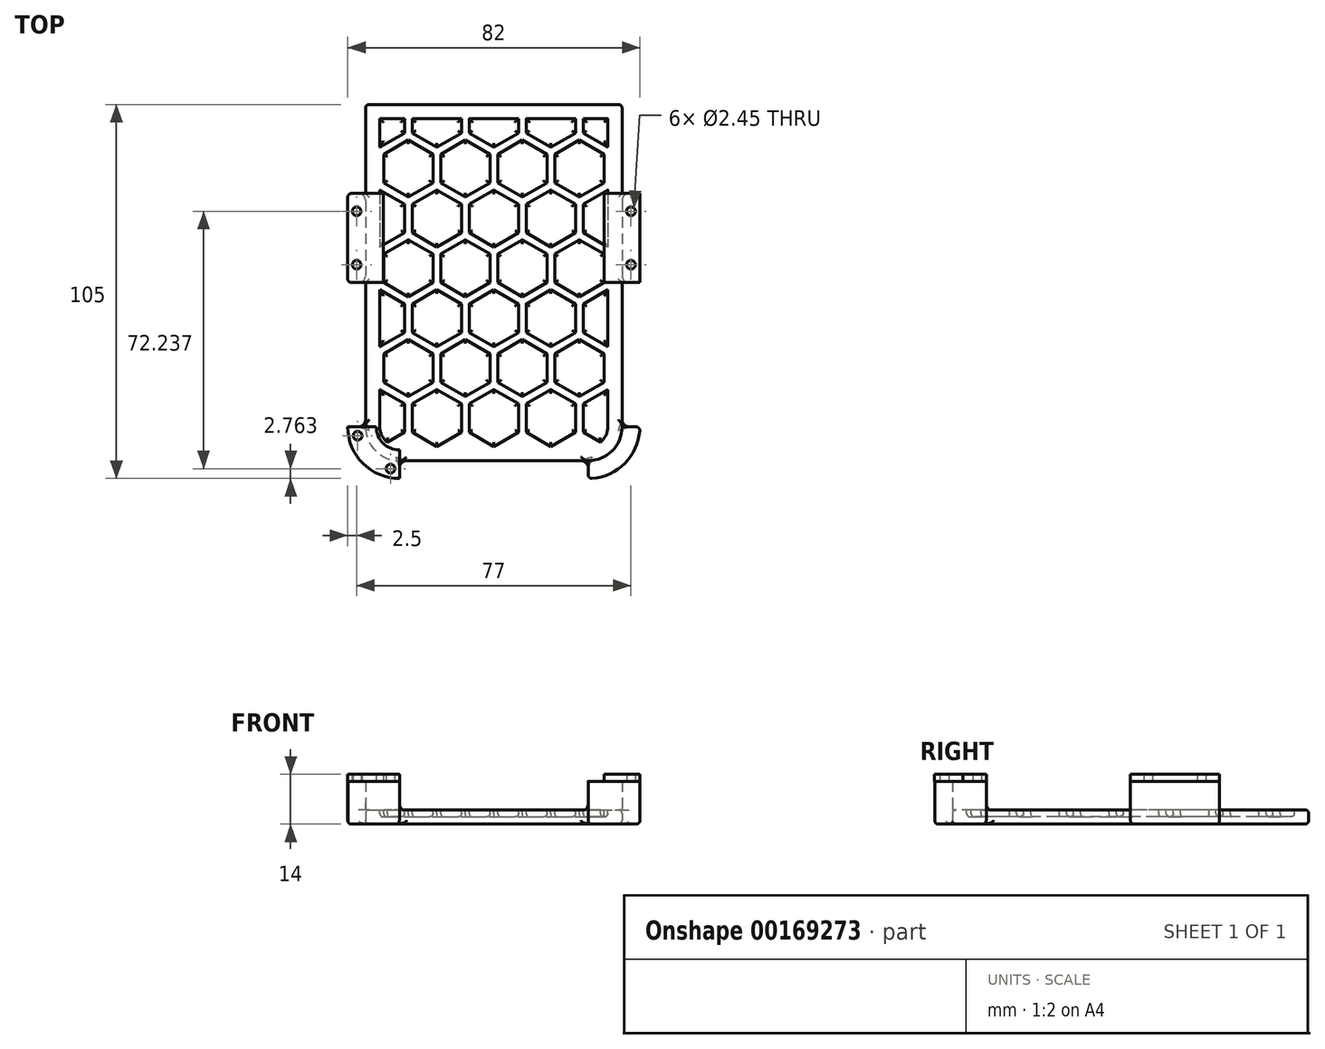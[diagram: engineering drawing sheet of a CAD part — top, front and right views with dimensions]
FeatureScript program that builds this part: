
annotation { "Feature Type Name" : "Feature", "Feature Type Description" : "" }
export const myFeature = defineFeature(function(context is Context, id is Id, definition is map)
    precondition{}
    {
        {
            var Q0;
            Q0=qCreatedBy(makeId("Top.planeOp"),FACE);
            var sketch = newSketch(context, id + "F0", { "sketchPlane" : qUnion([Q0])});
            skLineSegment(sketch, "E0.bottom", {"start": v(-36, 0) * mm, "end": v(36, 0) * mm});
            skLineSegment(sketch, "E0.top", {"start": v(-26.5, -100) * mm, "end": v(26.5, -100) * mm});
            skLineSegment(sketch, "E0.left", {"start": v(-36, 0) * mm, "end": v(-36, -90.5) * mm});
            skLineSegment(sketch, "E0.right", {"start": v(36, 0) * mm, "end": v(36, -90.5) * mm});
            skLineSegment(sketch, "E1", {"start": v(-36, -25) * mm, "end": v(-41, -25) * mm});
            skLineSegment(sketch, "E2", {"start": v(-41, -25) * mm, "end": v(-41, -50) * mm});
            skLineSegment(sketch, "E3", {"start": v(-41, -50) * mm, "end": v(-36, -50) * mm});
            skPoint(sketch, "E4.visualSharp", {"position": v(-36, -100) * mm});
            skArc(sketch, "E4.filletArc", {"start": v(-36, -90.5) * mm, "mid": v(-33.22, -97.22) * mm, "end": v(-26.5, -100) * mm});
            skPoint(sketch, "E5.visualSharp", {"position": v(36, -100) * mm});
            skArc(sketch, "E5.filletArc", {"start": v(26.5, -100) * mm, "mid": v(33.22, -97.22) * mm, "end": v(36, -90.5) * mm});
            skLineSegment(sketch, "E6", {"start": v(0, 0) * mm, "end": v(0, -100) * mm, "construction": true});
            skLineSegment(sketch, "E7.MirrorCS", {"start": v(36, -25) * mm, "end": v(41, -25) * mm});
            skLineSegment(sketch, "E8.MirrorCS", {"start": v(41, -25) * mm, "end": v(41, -50) * mm});
            skLineSegment(sketch, "E9.MirrorCS", {"start": v(41, -50) * mm, "end": v(36, -50) * mm});
            skArc(sketch, "E10.0", {"start": v(-41, -90.5) * mm, "mid": v(-36.75, -100.75) * mm, "end": v(-26.5, -105) * mm});
            skLineSegment(sketch, "E11", {"start": v(-41, -90.5) * mm, "end": v(-36, -90.5) * mm});
            skLineSegment(sketch, "E12", {"start": v(-26.5, -100) * mm, "end": v(-26.5, -105) * mm});
            skLineSegment(sketch, "E13.MirrorCS", {"start": v(26.5, -100) * mm, "end": v(26.5, -105) * mm});
            skArc(sketch, "E14.MirrorCS", {"start": v(41, -90.5) * mm, "mid": v(36.75, -100.75) * mm, "end": v(26.5, -105) * mm});
            skLineSegment(sketch, "E15.MirrorCS", {"start": v(41, -90.5) * mm, "end": v(36, -90.5) * mm});
            skSolve(sketch);
        }
        {
            var Q0;
            {var subQ3=sQuery(id+"F0.wireOp",EDGE,"E0.bottom");Q0=makeQuery(id+"F0.imprint","IMPRINT",FACE,{"disambiguationData":[TD([[makeQuery(id+"F0.imprint","IMPRINT",EDGE,{"derivedFrom":subQ3}),-1.0]])]});}
            extrude(context, id + "F1", {"entities" : qUnion([Q0]), "depth" : 4 * mm});
        }
        {
            var Q0;
            {var subQ0=sQuery(id+"F0.wireOp",EDGE,"E1");Q0=makeQuery(id+"F0.imprint","IMPRINT",FACE,{"disambiguationData":[TD([[makeQuery(id+"F0.imprint","IMPRINT",EDGE,{"derivedFrom":subQ0}),1.0]])]});}
            var Q1;
            Q1=makeQuery(id+"F0.imprint","IMPRINT",FACE,{"disambiguationData":[TD([[makeQuery(id+"F0.imprint","IMPRINT",EDGE,{"derivedFrom":sQuery(id+"F0.wireOp",EDGE,"E4.filletArc")}),-1.0]])]});
            var Q2;
            Q2=makeQuery(id+"F0.imprint","IMPRINT",FACE,{"disambiguationData":[TD([[makeQuery(id+"F0.imprint","IMPRINT",EDGE,{"derivedFrom":sQuery(id+"F0.wireOp",EDGE,"E5.filletArc")}),-1.0]])]});
            var Q3;
            {var subQ0=sQuery(id+"F0.wireOp",EDGE,"E7.MirrorCS");Q3=makeQuery(id+"F0.imprint","IMPRINT",FACE,{"disambiguationData":[TD([[makeQuery(id+"F0.imprint","IMPRINT",EDGE,{"derivedFrom":subQ0}),-1.0]])]});}
            extrude(context, id + "F2", {"entities" : qUnion([Q0, Q1, Q2, Q3]), "operationType" : NewBodyOperationType.ADD, "depth" : 12 * mm});
        }
        {
            var Q0;
            Q0=makeQuery(id+"F2.opExtrude","SWEPT_EDGE",EDGE,{"disambiguationData":[OSD([sQuery(id+"F0.wireOp",EDGE,"E2"),sQuery(id+"F0.wireOp",EDGE,"E3")])]});
            var Q1;
            Q1=makeQuery(id+"F2.opExtrude","SWEPT_EDGE",EDGE,{"disambiguationData":[OSD([sQuery(id+"F0.wireOp",EDGE,"E1"),sQuery(id+"F0.wireOp",EDGE,"E2")])]});
            var Q2;
            Q2=makeQuery(id+"F2.opExtrude","SWEPT_EDGE",EDGE,{"disambiguationData":[OSD([sQuery(id+"F0.wireOp",EDGE,"E10.0"),sQuery(id+"F0.wireOp",EDGE,"E11")])]});
            var Q3;
            Q3=makeQuery(id+"F2.opExtrude","SWEPT_EDGE",EDGE,{"disambiguationData":[OSD([sQuery(id+"F0.wireOp",EDGE,"E10.0"),sQuery(id+"F0.wireOp",EDGE,"E12")])]});
            var Q4;
            Q4=makeQuery(id+"F2.opExtrude","CAP_EDGE",EDGE,{"disambiguationData":[OSD([sQuery(id+"F0.wireOp",EDGE,"E10.0")])],"isStart":true});
            var Q5;
            Q5=makeQuery(id+"F2.opExtrude","CAP_EDGE",EDGE,{"disambiguationData":[OSD([sQuery(id+"F0.wireOp",EDGE,"E2")])],"isStart":true});
            var Q6;
            Q6=makeQuery(id+"F2.opExtrude","CAP_EDGE",EDGE,{"disambiguationData":[OSD([sQuery(id+"F0.wireOp",EDGE,"E14.MirrorCS")])],"isStart":true});
            var Q7;
            Q7=makeQuery(id+"F2.opExtrude","SWEPT_EDGE",EDGE,{"disambiguationData":[OSD([sQuery(id+"F0.wireOp",EDGE,"E13.MirrorCS"),sQuery(id+"F0.wireOp",EDGE,"E14.MirrorCS")])]});
            var Q8;
            Q8=makeQuery(id+"F2.opExtrude","SWEPT_EDGE",EDGE,{"disambiguationData":[OSD([sQuery(id+"F0.wireOp",EDGE,"E14.MirrorCS"),sQuery(id+"F0.wireOp",EDGE,"E15.MirrorCS")])]});
            var Q9;
            Q9=makeQuery(id+"F2.opExtrude","SWEPT_EDGE",EDGE,{"disambiguationData":[OSD([sQuery(id+"F0.wireOp",EDGE,"E8.MirrorCS"),sQuery(id+"F0.wireOp",EDGE,"E9.MirrorCS")])]});
            var Q10;
            Q10=makeQuery(id+"F2.opExtrude","SWEPT_EDGE",EDGE,{"disambiguationData":[OSD([sQuery(id+"F0.wireOp",EDGE,"E7.MirrorCS"),sQuery(id+"F0.wireOp",EDGE,"E8.MirrorCS")])]});
            var Q11;
            Q11=makeQuery(id+"F2.opExtrude","CAP_EDGE",EDGE,{"disambiguationData":[OSD([sQuery(id+"F0.wireOp",EDGE,"E8.MirrorCS")])],"isStart":true});
            var Q12;
            Q12=makeQuery(id+"F2.opExtrude","CAP_EDGE",EDGE,{"disambiguationData":[OSD([sQuery(id+"F0.wireOp",EDGE,"E9.MirrorCS")])],"isStart":true});
            var Q13;
            {var subQ1=sQuery(id+"F0.wireOp",EDGE,"E0.right");var subQ4=sQuery(id+"F0.wireOp",EDGE,"E0.bottom");Q13=makeQuery(id+"F2.boolean.opBoolean","SPLIT",EDGE,{"disambiguationData":[TD([makeQuery(id+"F1.opExtrude","SWEPT_FACE",FACE,{"disambiguationData":[OSD([subQ4])]})])],"derivedFrom":makeQuery(id+"F1.opExtrude","CAP_EDGE",EDGE,{"disambiguationData":[OSD([subQ1])],"isStart":true})});}
            var Q14;
            Q14=makeQuery(id+"F1.opExtrude","CAP_EDGE",EDGE,{"disambiguationData":[OSD([sQuery(id+"F0.wireOp",EDGE,"E0.top")])],"isStart":true});
            var Q15;
            {var subQ1=sQuery(id+"F0.wireOp",EDGE,"E0.left");var subQ2=sQuery(id+"F0.wireOp",EDGE,"E3");Q15=makeQuery(id+"F2.boolean.opBoolean","SPLIT",EDGE,{"disambiguationData":[TD([makeQuery(id+"F2.opExtrude","SWEPT_FACE",FACE,{"disambiguationData":[OSD([subQ2])]})])],"derivedFrom":makeQuery(id+"F1.opExtrude","CAP_EDGE",EDGE,{"disambiguationData":[OSD([subQ1])],"isStart":true})});}
            var Q16;
            Q16=makeQuery(id+"F2.opExtrude","CAP_EDGE",EDGE,{"disambiguationData":[OSD([sQuery(id+"F0.wireOp",EDGE,"E3")])],"isStart":true});
            var Q17;
            Q17=makeQuery(id+"F2.opExtrude","CAP_EDGE",EDGE,{"disambiguationData":[OSD([sQuery(id+"F0.wireOp",EDGE,"E1")])],"isStart":true});
            var Q18;
            Q18=makeQuery(id+"F1.opExtrude","SWEPT_EDGE",EDGE,{"disambiguationData":[OSD([sQuery(id+"F0.wireOp",EDGE,"E0.bottom"),sQuery(id+"F0.wireOp",EDGE,"E0.right")])]});
            var Q19;
            {var subQ0=sQuery(id+"F0.wireOp",EDGE,"E0.left");var subQ5=sQuery(id+"F0.wireOp",EDGE,"E0.bottom");Q19=makeQuery(id+"F2.boolean.opBoolean","SPLIT",EDGE,{"disambiguationData":[TD([makeQuery(id+"F1.opExtrude","SWEPT_FACE",FACE,{"disambiguationData":[OSD([subQ5])]})])],"derivedFrom":makeQuery(id+"F1.opExtrude","CAP_EDGE",EDGE,{"disambiguationData":[OSD([subQ0])],"isStart":true})});}
            var Q20;
            Q20=makeQuery(id+"F1.opExtrude","CAP_EDGE",EDGE,{"disambiguationData":[OSD([sQuery(id+"F0.wireOp",EDGE,"E0.bottom")])],"isStart":true});
            var Q21;
            {var subQ0=sQuery(id+"F0.wireOp",EDGE,"E0.left");var subQ1=sQuery(id+"F0.wireOp",EDGE,"E0.bottom");Q21=makeQuery(id+"F2.boolean.opBoolean","SPLIT",EDGE,{"disambiguationData":[TD([makeQuery(id+"F1.opExtrude","SWEPT_FACE",FACE,{"disambiguationData":[OSD([subQ1])]}),makeQuery(id+"F1.opExtrude","CAP_FACE",FACE,{"disambiguationData":[OSD([subQ1,sQuery(id+"F0.wireOp",EDGE,"E0.top"),subQ0,sQuery(id+"F0.wireOp",EDGE,"E0.right"),sQuery(id+"F0.wireOp",EDGE,"E4.filletArc"),sQuery(id+"F0.wireOp",EDGE,"E5.filletArc")])],"isStart":false}),makeQuery(id+"F1.opExtrude","SWEPT_FACE",FACE,{"disambiguationData":[OSD([subQ0])]}),makeQuery(id+"F2.opExtrude","SWEPT_FACE",FACE,{"disambiguationData":[OSD([subQ0])]}),makeQuery(id+"F2.opExtrude","SWEPT_FACE",FACE,{"disambiguationData":[OSD([sQuery(id+"F0.wireOp",EDGE,"E1")])]})])],"derivedFrom":makeQuery(id+"F1.opExtrude","CAP_EDGE",EDGE,{"disambiguationData":[OSD([subQ0])],"isStart":false})});}
            var Q22;
            Q22=makeQuery(id+"F1.opExtrude","SWEPT_EDGE",EDGE,{"disambiguationData":[OSD([sQuery(id+"F0.wireOp",EDGE,"E0.bottom"),sQuery(id+"F0.wireOp",EDGE,"E0.left")])]});
            var Q23;
            Q23=makeQuery(id+"F1.opExtrude","CAP_EDGE",EDGE,{"disambiguationData":[OSD([sQuery(id+"F0.wireOp",EDGE,"E0.bottom")])],"isStart":false});
            var Q24;
            {var subQ0=sQuery(id+"F0.wireOp",EDGE,"E0.right");var subQ1=sQuery(id+"F0.wireOp",EDGE,"E0.bottom");Q24=makeQuery(id+"F2.boolean.opBoolean","SPLIT",EDGE,{"disambiguationData":[TD([makeQuery(id+"F1.opExtrude","SWEPT_FACE",FACE,{"disambiguationData":[OSD([subQ1])]}),makeQuery(id+"F1.opExtrude","CAP_FACE",FACE,{"disambiguationData":[OSD([subQ1,sQuery(id+"F0.wireOp",EDGE,"E0.top"),sQuery(id+"F0.wireOp",EDGE,"E0.left"),subQ0,sQuery(id+"F0.wireOp",EDGE,"E4.filletArc"),sQuery(id+"F0.wireOp",EDGE,"E5.filletArc")])],"isStart":false}),makeQuery(id+"F1.opExtrude","SWEPT_FACE",FACE,{"disambiguationData":[OSD([subQ0])]}),makeQuery(id+"F2.opExtrude","SWEPT_FACE",FACE,{"disambiguationData":[OSD([subQ0])]}),makeQuery(id+"F2.opExtrude","SWEPT_FACE",FACE,{"disambiguationData":[OSD([sQuery(id+"F0.wireOp",EDGE,"E7.MirrorCS")])]})])],"derivedFrom":makeQuery(id+"F1.opExtrude","CAP_EDGE",EDGE,{"disambiguationData":[OSD([subQ0])],"isStart":false})});}
            var Q25;
            {var subQ0=sQuery(id+"F0.wireOp",EDGE,"E5.filletArc");var subQ1=sQuery(id+"F0.wireOp",EDGE,"E0.right");Q25=makeQuery(id+"F2.boolean.opBoolean","SPLIT",EDGE,{"disambiguationData":[TD([makeQuery(id+"F1.opExtrude","CAP_FACE",FACE,{"disambiguationData":[OSD([sQuery(id+"F0.wireOp",EDGE,"E0.bottom"),sQuery(id+"F0.wireOp",EDGE,"E0.top"),sQuery(id+"F0.wireOp",EDGE,"E0.left"),subQ1,sQuery(id+"F0.wireOp",EDGE,"E4.filletArc"),subQ0])],"isStart":false}),makeQuery(id+"F1.opExtrude","SWEPT_FACE",FACE,{"disambiguationData":[OSD([subQ1])]}),makeQuery(id+"F2.opExtrude","SWEPT_FACE",FACE,{"disambiguationData":[OSD([subQ1])]}),makeQuery(id+"F2.opExtrude","SWEPT_FACE",FACE,{"disambiguationData":[OSD([subQ0])]}),makeQuery(id+"F2.opExtrude","SWEPT_FACE",FACE,{"disambiguationData":[OSD([sQuery(id+"F0.wireOp",EDGE,"E9.MirrorCS")])]}),makeQuery(id+"F2.opExtrude","SWEPT_FACE",FACE,{"disambiguationData":[OSD([sQuery(id+"F0.wireOp",EDGE,"E15.MirrorCS")])]})])],"derivedFrom":makeQuery(id+"F1.opExtrude","CAP_EDGE",EDGE,{"disambiguationData":[OSD([subQ1])],"isStart":false})});}
            var Q26;
            Q26=makeQuery(id+"F1.opExtrude","CAP_EDGE",EDGE,{"disambiguationData":[OSD([sQuery(id+"F0.wireOp",EDGE,"E0.top")])],"isStart":false});
            var Q27;
            {var subQ0=sQuery(id+"F0.wireOp",EDGE,"E0.left");var subQ1=sQuery(id+"F0.wireOp",EDGE,"E4.filletArc");Q27=makeQuery(id+"F2.boolean.opBoolean","SPLIT",EDGE,{"disambiguationData":[TD([makeQuery(id+"F1.opExtrude","CAP_FACE",FACE,{"disambiguationData":[OSD([sQuery(id+"F0.wireOp",EDGE,"E0.bottom"),sQuery(id+"F0.wireOp",EDGE,"E0.top"),subQ0,sQuery(id+"F0.wireOp",EDGE,"E0.right"),subQ1,sQuery(id+"F0.wireOp",EDGE,"E5.filletArc")])],"isStart":false}),makeQuery(id+"F1.opExtrude","SWEPT_FACE",FACE,{"disambiguationData":[OSD([subQ0])]}),makeQuery(id+"F2.opExtrude","SWEPT_FACE",FACE,{"disambiguationData":[OSD([subQ0])]}),makeQuery(id+"F2.opExtrude","SWEPT_FACE",FACE,{"disambiguationData":[OSD([sQuery(id+"F0.wireOp",EDGE,"E3")])]}),makeQuery(id+"F2.opExtrude","SWEPT_FACE",FACE,{"disambiguationData":[OSD([subQ1])]}),makeQuery(id+"F2.opExtrude","SWEPT_FACE",FACE,{"disambiguationData":[OSD([sQuery(id+"F0.wireOp",EDGE,"E11")])]})])],"derivedFrom":makeQuery(id+"F1.opExtrude","CAP_EDGE",EDGE,{"disambiguationData":[OSD([subQ0])],"isStart":false})});}
            var Q28;
            Q28=makeQuery(id+"F2.opExtrude","CAP_EDGE",EDGE,{"disambiguationData":[OSD([sQuery(id+"F0.wireOp",EDGE,"E11")])],"isStart":true});
            var Q29;
            Q29=makeQuery(id+"F2.opExtrude","CAP_EDGE",EDGE,{"disambiguationData":[OSD([sQuery(id+"F0.wireOp",EDGE,"E12")])],"isStart":true});
            var Q30;
            Q30=makeQuery(id+"F2.opExtrude","CAP_EDGE",EDGE,{"disambiguationData":[OSD([sQuery(id+"F0.wireOp",EDGE,"E13.MirrorCS")])],"isStart":true});
            var Q31;
            {var subQ0=sQuery(id+"F0.wireOp",EDGE,"E9.MirrorCS");var subQ1=sQuery(id+"F0.wireOp",EDGE,"E0.right");Q31=makeQuery(id+"F2.boolean.opBoolean","SPLIT",EDGE,{"disambiguationData":[TD([makeQuery(id+"F2.opExtrude","SWEPT_FACE",FACE,{"disambiguationData":[OSD([subQ0])]})])],"derivedFrom":makeQuery(id+"F1.opExtrude","CAP_EDGE",EDGE,{"disambiguationData":[OSD([subQ1])],"isStart":true})});}
            var Q32;
            Q32=makeQuery(id+"F2.opExtrude","CAP_EDGE",EDGE,{"disambiguationData":[OSD([sQuery(id+"F0.wireOp",EDGE,"E15.MirrorCS")])],"isStart":true});
            var Q33;
            Q33=makeQuery(id+"F2.opExtrude","CAP_EDGE",EDGE,{"disambiguationData":[OSD([sQuery(id+"F0.wireOp",EDGE,"E7.MirrorCS")])],"isStart":true});
            fillet(context, id + "F3", {"entities" : qUnion([Q0, Q1, Q2, Q3, Q4, Q5, Q6, Q7, Q8, Q9, Q10, Q11, Q12, Q13, Q14, Q15, Q16, Q17, Q18, Q19, Q20, Q21, Q22, Q23, Q24, Q25, Q26, Q27, Q28, Q29, Q30, Q31, Q32, Q33]), "radius" : 1 * mm, "tangentPropagation" : true, "allowEdgeOverflow" : false});
        }
        {
            var Q0;
            {var subQ0=sQuery(id+"F0.wireOp",EDGE,"E0.left");var subQ6=sQuery(id+"F0.wireOp",EDGE,"E3");Q0=makeQuery(id+"F2.boolean.opBoolean","SPLIT",EDGE,{"disambiguationData":[TD([makeQuery(id+"F2.opExtrude","CAP_FACE",FACE,{"disambiguationData":[OSD([subQ0,sQuery(id+"F0.wireOp",EDGE,"E1"),sQuery(id+"F0.wireOp",EDGE,"E2"),subQ6])],"isStart":true})])],"derivedFrom":makeQuery(id+"F2.opExtrude","SWEPT_EDGE",EDGE,{"disambiguationData":[OSD([subQ0,subQ6])]})});}
            var Q1;
            {var subQ0=sQuery(id+"F0.wireOp",EDGE,"E11");var subQ1=sQuery(id+"F0.wireOp",EDGE,"E4.filletArc");var subQ2=sQuery(id+"F0.wireOp",EDGE,"E0.left");Q1=makeQuery(id+"F2.boolean.opBoolean","MERGE",EDGE,{"derivedFrom":[makeQuery(id+"F1.opExtrude","SWEPT_EDGE",EDGE,{"disambiguationData":[OSD([subQ2,subQ1,subQ0])]}),makeQuery(id+"F2.opExtrude","SWEPT_EDGE",EDGE,{"disambiguationData":[OSD([subQ2,subQ1,subQ0])]})]});}
            var Q2;
            {var subQ0=sQuery(id+"F0.wireOp",EDGE,"E13.MirrorCS");var subQ1=sQuery(id+"F0.wireOp",EDGE,"E5.filletArc");var subQ2=sQuery(id+"F0.wireOp",EDGE,"E0.top");Q2=makeQuery(id+"F2.boolean.opBoolean","MERGE",EDGE,{"derivedFrom":[makeQuery(id+"F1.opExtrude","SWEPT_EDGE",EDGE,{"disambiguationData":[OSD([subQ2,subQ1,subQ0])]}),makeQuery(id+"F2.opExtrude","SWEPT_EDGE",EDGE,{"disambiguationData":[OSD([subQ2,subQ1,subQ0])]})]});}
            var Q3;
            {var subQ0=sQuery(id+"F0.wireOp",EDGE,"E12");var subQ1=sQuery(id+"F0.wireOp",EDGE,"E4.filletArc");var subQ2=sQuery(id+"F0.wireOp",EDGE,"E0.top");Q3=makeQuery(id+"F2.boolean.opBoolean","MERGE",EDGE,{"derivedFrom":[makeQuery(id+"F1.opExtrude","SWEPT_EDGE",EDGE,{"disambiguationData":[OSD([subQ2,subQ1,subQ0])]}),makeQuery(id+"F2.opExtrude","SWEPT_EDGE",EDGE,{"disambiguationData":[OSD([subQ2,subQ1,subQ0])]})]});}
            var Q4;
            {var subQ0=sQuery(id+"F0.wireOp",EDGE,"E0.right");var subQ1=sQuery(id+"F0.wireOp",EDGE,"E0.left");var subQ6=sQuery(id+"F0.wireOp",EDGE,"E9.MirrorCS");Q4=makeQuery(id+"F2.boolean.opBoolean","SPLIT",EDGE,{"disambiguationData":[TD([makeQuery(id+"F2.opExtrude","CAP_FACE",FACE,{"disambiguationData":[OSD([subQ1,sQuery(id+"F0.wireOp",EDGE,"E1"),sQuery(id+"F0.wireOp",EDGE,"E2"),sQuery(id+"F0.wireOp",EDGE,"E3")])],"isStart":true})])],"derivedFrom":makeQuery(id+"F2.opExtrude","SWEPT_EDGE",EDGE,{"disambiguationData":[OSD([subQ0,subQ6])]})});}
            var Q5;
            {var subQ0=sQuery(id+"F0.wireOp",EDGE,"E15.MirrorCS");var subQ1=sQuery(id+"F0.wireOp",EDGE,"E5.filletArc");var subQ2=sQuery(id+"F0.wireOp",EDGE,"E0.right");Q5=makeQuery(id+"F2.boolean.opBoolean","MERGE",EDGE,{"derivedFrom":[makeQuery(id+"F1.opExtrude","SWEPT_EDGE",EDGE,{"disambiguationData":[OSD([subQ2,subQ1,subQ0])]}),makeQuery(id+"F2.opExtrude","SWEPT_EDGE",EDGE,{"disambiguationData":[OSD([subQ2,subQ1,subQ0])]})]});}
            var Q6;
            {var subQ0=sQuery(id+"F0.wireOp",EDGE,"E0.right");var subQ1=sQuery(id+"F0.wireOp",EDGE,"E0.left");var subQ6=sQuery(id+"F0.wireOp",EDGE,"E7.MirrorCS");Q6=makeQuery(id+"F2.boolean.opBoolean","SPLIT",EDGE,{"disambiguationData":[TD([makeQuery(id+"F2.opExtrude","CAP_FACE",FACE,{"disambiguationData":[OSD([subQ1,sQuery(id+"F0.wireOp",EDGE,"E1"),sQuery(id+"F0.wireOp",EDGE,"E2"),sQuery(id+"F0.wireOp",EDGE,"E3")])],"isStart":true})])],"derivedFrom":makeQuery(id+"F2.opExtrude","SWEPT_EDGE",EDGE,{"disambiguationData":[OSD([subQ0,subQ6])]})});}
            var Q7;
            {var subQ0=sQuery(id+"F0.wireOp",EDGE,"E0.left");var subQ6=sQuery(id+"F0.wireOp",EDGE,"E1");Q7=makeQuery(id+"F2.boolean.opBoolean","SPLIT",EDGE,{"disambiguationData":[TD([makeQuery(id+"F2.opExtrude","CAP_FACE",FACE,{"disambiguationData":[OSD([subQ0,subQ6,sQuery(id+"F0.wireOp",EDGE,"E2"),sQuery(id+"F0.wireOp",EDGE,"E3")])],"isStart":true})])],"derivedFrom":makeQuery(id+"F2.opExtrude","SWEPT_EDGE",EDGE,{"disambiguationData":[OSD([subQ0,subQ6])]})});}
            fillet(context, id + "F4", {"entities" : qUnion([Q0, Q1, Q2, Q3, Q4, Q5, Q6, Q7]), "radius" : 2 * mm, "tangentPropagation" : true, "allowEdgeOverflow" : false});
        }
        {
            var Q0;
            Q0=makeQuery(id+"F1.opExtrude","CAP_FACE",FACE,{"disambiguationData":[OSD([sQuery(id+"F0.wireOp",EDGE,"E0.bottom"),sQuery(id+"F0.wireOp",EDGE,"E0.top"),sQuery(id+"F0.wireOp",EDGE,"E0.left"),sQuery(id+"F0.wireOp",EDGE,"E0.right"),sQuery(id+"F0.wireOp",EDGE,"E4.filletArc"),sQuery(id+"F0.wireOp",EDGE,"E5.filletArc")])],"isStart":false});
            var sketch = newSketch(context, id + "F5", { "sketchPlane" : qUnion([Q0])});
            skLineSegment(sketch, "E16.0", {"start": v(-32, -4) * mm, "end": v(-32, -90.5) * mm});
            skLineSegment(sketch, "E16.1", {"start": v(32, -4) * mm, "end": v(32, -90.5) * mm});
            skArc(sketch, "E16.2", {"start": v(26.5, -96) * mm, "mid": v(30.39, -94.39) * mm, "end": v(32, -90.5) * mm});
            skLineSegment(sketch, "E16.3", {"start": v(-32, -4) * mm, "end": v(32, -4) * mm});
            skLineSegment(sketch, "E16.4", {"start": v(-26.5, -96) * mm, "end": v(26.5, -96) * mm});
            skArc(sketch, "E16.5", {"start": v(-32, -90.5) * mm, "mid": v(-30.39, -94.39) * mm, "end": v(-26.5, -96) * mm});
            skCircle(sketch, "E17.cCircle", {"center": v(-32, -4) * mm, "radius": 8 * mm, "construction": true});
            skLineSegment(sketch, "E17.0", {"start": v(-25.07, 0) * mm, "end": v(-25.07, -8) * mm});
            skLineSegment(sketch, "E17.1", {"start": v(-25.07, -8) * mm, "end": v(-32, -12) * mm});
            skLineSegment(sketch, "E17.2", {"start": v(-32, -12) * mm, "end": v(-38.93, -8) * mm});
            skLineSegment(sketch, "E17.3", {"start": v(-38.93, -8) * mm, "end": v(-38.93, 0) * mm});
            skLineSegment(sketch, "E17.4", {"start": v(-38.93, 0) * mm, "end": v(-32, 4) * mm});
            skLineSegment(sketch, "E17.5", {"start": v(-32, 4) * mm, "end": v(-25.07, 0) * mm});
            skLineSegment(sketch, "E18.0.1.0", {"start": v(-32, -24) * mm, "end": v(-25.07, -28) * mm});
            skLineSegment(sketch, "E18.0.1.1", {"start": v(-25.07, -28) * mm, "end": v(-25.07, -36) * mm});
            skLineSegment(sketch, "E18.0.1.2", {"start": v(-25.07, -36) * mm, "end": v(-32, -40) * mm});
            skLineSegment(sketch, "E18.0.1.3", {"start": v(-32, -40) * mm, "end": v(-38.93, -36) * mm});
            skLineSegment(sketch, "E18.0.1.4", {"start": v(-38.93, -36) * mm, "end": v(-38.93, -28) * mm});
            skLineSegment(sketch, "E18.0.1.5", {"start": v(-38.93, -28) * mm, "end": v(-32, -24) * mm});
            skLineSegment(sketch, "E18.0.2.0", {"start": v(-32, -52) * mm, "end": v(-25.07, -56) * mm});
            skLineSegment(sketch, "E18.0.2.1", {"start": v(-25.07, -56) * mm, "end": v(-25.07, -64) * mm});
            skLineSegment(sketch, "E18.0.2.2", {"start": v(-25.07, -64) * mm, "end": v(-32, -68) * mm});
            skLineSegment(sketch, "E18.0.2.3", {"start": v(-32, -68) * mm, "end": v(-38.93, -64) * mm});
            skLineSegment(sketch, "E18.0.2.4", {"start": v(-38.93, -64) * mm, "end": v(-38.93, -56) * mm});
            skLineSegment(sketch, "E18.0.2.5", {"start": v(-38.93, -56) * mm, "end": v(-32, -52) * mm});
            skLineSegment(sketch, "E18.0.3.0", {"start": v(-32, -80) * mm, "end": v(-25.07, -84) * mm});
            skLineSegment(sketch, "E18.0.3.1", {"start": v(-25.07, -84) * mm, "end": v(-25.07, -92) * mm});
            skLineSegment(sketch, "E18.0.3.2", {"start": v(-25.07, -92) * mm, "end": v(-32, -96) * mm});
            skLineSegment(sketch, "E18.0.3.3", {"start": v(-32, -96) * mm, "end": v(-38.93, -92) * mm});
            skLineSegment(sketch, "E18.0.3.4", {"start": v(-38.93, -92) * mm, "end": v(-38.93, -84) * mm});
            skLineSegment(sketch, "E18.0.3.5", {"start": v(-38.93, -84) * mm, "end": v(-32, -80) * mm});
            skLineSegment(sketch, "E18.1.0.0", {"start": v(-16, 4) * mm, "end": v(-9.07, 0) * mm});
            skLineSegment(sketch, "E18.1.0.1", {"start": v(-9.07, 0) * mm, "end": v(-9.07, -8) * mm});
            skLineSegment(sketch, "E18.1.0.2", {"start": v(-9.07, -8) * mm, "end": v(-16, -12) * mm});
            skLineSegment(sketch, "E18.1.0.3", {"start": v(-16, -12) * mm, "end": v(-22.93, -8) * mm});
            skLineSegment(sketch, "E18.1.0.4", {"start": v(-22.93, -8) * mm, "end": v(-22.93, 0) * mm});
            skLineSegment(sketch, "E18.1.0.5", {"start": v(-22.93, 0) * mm, "end": v(-16, 4) * mm});
            skLineSegment(sketch, "E18.1.1.0", {"start": v(-16, -24) * mm, "end": v(-9.07, -28) * mm});
            skLineSegment(sketch, "E18.1.1.1", {"start": v(-9.07, -28) * mm, "end": v(-9.07, -36) * mm});
            skLineSegment(sketch, "E18.1.1.2", {"start": v(-9.07, -36) * mm, "end": v(-16, -40) * mm});
            skLineSegment(sketch, "E18.1.1.3", {"start": v(-16, -40) * mm, "end": v(-22.93, -36) * mm});
            skLineSegment(sketch, "E18.1.1.4", {"start": v(-22.93, -36) * mm, "end": v(-22.93, -28) * mm});
            skLineSegment(sketch, "E18.1.1.5", {"start": v(-22.93, -28) * mm, "end": v(-16, -24) * mm});
            skLineSegment(sketch, "E18.1.2.0", {"start": v(-16, -52) * mm, "end": v(-9.07, -56) * mm});
            skLineSegment(sketch, "E18.1.2.1", {"start": v(-9.07, -56) * mm, "end": v(-9.07, -64) * mm});
            skLineSegment(sketch, "E18.1.2.2", {"start": v(-9.07, -64) * mm, "end": v(-16, -68) * mm});
            skLineSegment(sketch, "E18.1.2.3", {"start": v(-16, -68) * mm, "end": v(-22.93, -64) * mm});
            skLineSegment(sketch, "E18.1.2.4", {"start": v(-22.93, -64) * mm, "end": v(-22.93, -56) * mm});
            skLineSegment(sketch, "E18.1.2.5", {"start": v(-22.93, -56) * mm, "end": v(-16, -52) * mm});
            skLineSegment(sketch, "E18.1.3.0", {"start": v(-16, -80) * mm, "end": v(-9.07, -84) * mm});
            skLineSegment(sketch, "E18.1.3.1", {"start": v(-9.07, -84) * mm, "end": v(-9.07, -92) * mm});
            skLineSegment(sketch, "E18.1.3.2", {"start": v(-9.07, -92) * mm, "end": v(-16, -96) * mm});
            skLineSegment(sketch, "E18.1.3.3", {"start": v(-16, -96) * mm, "end": v(-22.93, -92) * mm});
            skLineSegment(sketch, "E18.1.3.4", {"start": v(-22.93, -92) * mm, "end": v(-22.93, -84) * mm});
            skLineSegment(sketch, "E18.1.3.5", {"start": v(-22.93, -84) * mm, "end": v(-16, -80) * mm});
            skLineSegment(sketch, "E18.2.0.0", {"start": v(0, 4) * mm, "end": v(6.93, 0) * mm});
            skLineSegment(sketch, "E18.2.0.1", {"start": v(6.93, 0) * mm, "end": v(6.93, -8) * mm});
            skLineSegment(sketch, "E18.2.0.2", {"start": v(6.93, -8) * mm, "end": v(0, -12) * mm});
            skLineSegment(sketch, "E18.2.0.3", {"start": v(0, -12) * mm, "end": v(-6.93, -8) * mm});
            skLineSegment(sketch, "E18.2.0.4", {"start": v(-6.93, -8) * mm, "end": v(-6.93, 0) * mm});
            skLineSegment(sketch, "E18.2.0.5", {"start": v(-6.93, 0) * mm, "end": v(0, 4) * mm});
            skLineSegment(sketch, "E18.2.1.0", {"start": v(0, -24) * mm, "end": v(6.93, -28) * mm});
            skLineSegment(sketch, "E18.2.1.1", {"start": v(6.93, -28) * mm, "end": v(6.93, -36) * mm});
            skLineSegment(sketch, "E18.2.1.2", {"start": v(6.93, -36) * mm, "end": v(0, -40) * mm});
            skLineSegment(sketch, "E18.2.1.3", {"start": v(0, -40) * mm, "end": v(-6.93, -36) * mm});
            skLineSegment(sketch, "E18.2.1.4", {"start": v(-6.93, -36) * mm, "end": v(-6.93, -28) * mm});
            skLineSegment(sketch, "E18.2.1.5", {"start": v(-6.93, -28) * mm, "end": v(0, -24) * mm});
            skLineSegment(sketch, "E18.2.2.0", {"start": v(0, -52) * mm, "end": v(6.93, -56) * mm});
            skLineSegment(sketch, "E18.2.2.1", {"start": v(6.93, -56) * mm, "end": v(6.93, -64) * mm});
            skLineSegment(sketch, "E18.2.2.2", {"start": v(6.93, -64) * mm, "end": v(0, -68) * mm});
            skLineSegment(sketch, "E18.2.2.3", {"start": v(0, -68) * mm, "end": v(-6.93, -64) * mm});
            skLineSegment(sketch, "E18.2.2.4", {"start": v(-6.93, -64) * mm, "end": v(-6.93, -56) * mm});
            skLineSegment(sketch, "E18.2.2.5", {"start": v(-6.93, -56) * mm, "end": v(0, -52) * mm});
            skLineSegment(sketch, "E18.2.3.0", {"start": v(0, -80) * mm, "end": v(6.93, -84) * mm});
            skLineSegment(sketch, "E18.2.3.1", {"start": v(6.93, -84) * mm, "end": v(6.93, -92) * mm});
            skLineSegment(sketch, "E18.2.3.2", {"start": v(6.93, -92) * mm, "end": v(0, -96) * mm});
            skLineSegment(sketch, "E18.2.3.3", {"start": v(0, -96) * mm, "end": v(-6.93, -92) * mm});
            skLineSegment(sketch, "E18.2.3.4", {"start": v(-6.93, -92) * mm, "end": v(-6.93, -84) * mm});
            skLineSegment(sketch, "E18.2.3.5", {"start": v(-6.93, -84) * mm, "end": v(0, -80) * mm});
            skLineSegment(sketch, "E18.3.0.0", {"start": v(16, 4) * mm, "end": v(22.93, 0) * mm});
            skLineSegment(sketch, "E18.3.0.1", {"start": v(22.93, 0) * mm, "end": v(22.93, -8) * mm});
            skLineSegment(sketch, "E18.3.0.2", {"start": v(22.93, -8) * mm, "end": v(16, -12) * mm});
            skLineSegment(sketch, "E18.3.0.3", {"start": v(16, -12) * mm, "end": v(9.07, -8) * mm});
            skLineSegment(sketch, "E18.3.0.4", {"start": v(9.07, -8) * mm, "end": v(9.07, 0) * mm});
            skLineSegment(sketch, "E18.3.0.5", {"start": v(9.07, 0) * mm, "end": v(16, 4) * mm});
            skLineSegment(sketch, "E18.3.1.0", {"start": v(16, -24) * mm, "end": v(22.93, -28) * mm});
            skLineSegment(sketch, "E18.3.1.1", {"start": v(22.93, -28) * mm, "end": v(22.93, -36) * mm});
            skLineSegment(sketch, "E18.3.1.2", {"start": v(22.93, -36) * mm, "end": v(16, -40) * mm});
            skLineSegment(sketch, "E18.3.1.3", {"start": v(16, -40) * mm, "end": v(9.07, -36) * mm});
            skLineSegment(sketch, "E18.3.1.4", {"start": v(9.07, -36) * mm, "end": v(9.07, -28) * mm});
            skLineSegment(sketch, "E18.3.1.5", {"start": v(9.07, -28) * mm, "end": v(16, -24) * mm});
            skLineSegment(sketch, "E18.3.2.0", {"start": v(16, -52) * mm, "end": v(22.93, -56) * mm});
            skLineSegment(sketch, "E18.3.2.1", {"start": v(22.93, -56) * mm, "end": v(22.93, -64) * mm});
            skLineSegment(sketch, "E18.3.2.2", {"start": v(22.93, -64) * mm, "end": v(16, -68) * mm});
            skLineSegment(sketch, "E18.3.2.3", {"start": v(16, -68) * mm, "end": v(9.07, -64) * mm});
            skLineSegment(sketch, "E18.3.2.4", {"start": v(9.07, -64) * mm, "end": v(9.07, -56) * mm});
            skLineSegment(sketch, "E18.3.2.5", {"start": v(9.07, -56) * mm, "end": v(16, -52) * mm});
            skLineSegment(sketch, "E18.3.3.0", {"start": v(16, -80) * mm, "end": v(22.93, -84) * mm});
            skLineSegment(sketch, "E18.3.3.1", {"start": v(22.93, -84) * mm, "end": v(22.93, -92) * mm});
            skLineSegment(sketch, "E18.3.3.2", {"start": v(22.93, -92) * mm, "end": v(16, -96) * mm});
            skLineSegment(sketch, "E18.3.3.3", {"start": v(16, -96) * mm, "end": v(9.07, -92) * mm});
            skLineSegment(sketch, "E18.3.3.4", {"start": v(9.07, -92) * mm, "end": v(9.07, -84) * mm});
            skLineSegment(sketch, "E18.3.3.5", {"start": v(9.07, -84) * mm, "end": v(16, -80) * mm});
            skLineSegment(sketch, "E18.4.0.0", {"start": v(32, 4) * mm, "end": v(38.93, 0) * mm});
            skLineSegment(sketch, "E18.4.0.1", {"start": v(38.93, 0) * mm, "end": v(38.93, -8) * mm});
            skLineSegment(sketch, "E18.4.0.2", {"start": v(38.93, -8) * mm, "end": v(32, -12) * mm});
            skLineSegment(sketch, "E18.4.0.3", {"start": v(32, -12) * mm, "end": v(25.07, -8) * mm});
            skLineSegment(sketch, "E18.4.0.4", {"start": v(25.07, -8) * mm, "end": v(25.07, 0) * mm});
            skLineSegment(sketch, "E18.4.0.5", {"start": v(25.07, 0) * mm, "end": v(32, 4) * mm});
            skLineSegment(sketch, "E18.4.1.0", {"start": v(32, -24) * mm, "end": v(38.93, -28) * mm});
            skLineSegment(sketch, "E18.4.1.1", {"start": v(38.93, -28) * mm, "end": v(38.93, -36) * mm});
            skLineSegment(sketch, "E18.4.1.2", {"start": v(38.93, -36) * mm, "end": v(32, -40) * mm});
            skLineSegment(sketch, "E18.4.1.3", {"start": v(32, -40) * mm, "end": v(25.07, -36) * mm});
            skLineSegment(sketch, "E18.4.1.4", {"start": v(25.07, -36) * mm, "end": v(25.07, -28) * mm});
            skLineSegment(sketch, "E18.4.1.5", {"start": v(25.07, -28) * mm, "end": v(32, -24) * mm});
            skLineSegment(sketch, "E18.4.2.0", {"start": v(32, -52) * mm, "end": v(38.93, -56) * mm});
            skLineSegment(sketch, "E18.4.2.1", {"start": v(38.93, -56) * mm, "end": v(38.93, -64) * mm});
            skLineSegment(sketch, "E18.4.2.2", {"start": v(38.93, -64) * mm, "end": v(32, -68) * mm});
            skLineSegment(sketch, "E18.4.2.3", {"start": v(32, -68) * mm, "end": v(25.07, -64) * mm});
            skLineSegment(sketch, "E18.4.2.4", {"start": v(25.07, -64) * mm, "end": v(25.07, -56) * mm});
            skLineSegment(sketch, "E18.4.2.5", {"start": v(25.07, -56) * mm, "end": v(32, -52) * mm});
            skLineSegment(sketch, "E18.4.3.0", {"start": v(32, -80) * mm, "end": v(38.93, -84) * mm});
            skLineSegment(sketch, "E18.4.3.1", {"start": v(38.93, -84) * mm, "end": v(38.93, -92) * mm});
            skLineSegment(sketch, "E18.4.3.2", {"start": v(38.93, -92) * mm, "end": v(32, -96) * mm});
            skLineSegment(sketch, "E18.4.3.3", {"start": v(32, -96) * mm, "end": v(25.07, -92) * mm});
            skLineSegment(sketch, "E18.4.3.4", {"start": v(25.07, -92) * mm, "end": v(25.07, -84) * mm});
            skLineSegment(sketch, "E18.4.3.5", {"start": v(25.07, -84) * mm, "end": v(32, -80) * mm});
            skLineSegment(sketch, "E18.direction1", {"start": v(-32, 4) * mm, "end": v(-16, 4) * mm, "construction": true});
            skLineSegment(sketch, "E18.direction2", {"start": v(-32, 4) * mm, "end": v(-32, -24) * mm, "construction": true});
            skCircle(sketch, "E19.cCircle", {"center": v(-24, -18) * mm, "radius": 8 * mm, "construction": true});
            skLineSegment(sketch, "E19.0", {"start": v(-17.07, -22) * mm, "end": v(-24, -26) * mm});
            skLineSegment(sketch, "E19.1", {"start": v(-24, -26) * mm, "end": v(-30.93, -22) * mm});
            skLineSegment(sketch, "E19.2", {"start": v(-30.93, -22) * mm, "end": v(-30.93, -14) * mm});
            skLineSegment(sketch, "E19.3", {"start": v(-30.93, -14) * mm, "end": v(-24, -10) * mm});
            skLineSegment(sketch, "E19.4", {"start": v(-24, -10) * mm, "end": v(-17.07, -14) * mm});
            skLineSegment(sketch, "E19.5", {"start": v(-17.07, -14) * mm, "end": v(-17.07, -22) * mm});
            skLineSegment(sketch, "E20.0.1.0", {"start": v(-17.07, -42) * mm, "end": v(-17.07, -50) * mm});
            skLineSegment(sketch, "E20.0.1.1", {"start": v(-17.07, -50) * mm, "end": v(-24, -54) * mm});
            skLineSegment(sketch, "E20.0.1.2", {"start": v(-24, -54) * mm, "end": v(-30.93, -50) * mm});
            skLineSegment(sketch, "E20.0.1.3", {"start": v(-30.93, -50) * mm, "end": v(-30.93, -42) * mm});
            skLineSegment(sketch, "E20.0.1.4", {"start": v(-30.93, -42) * mm, "end": v(-24, -38) * mm});
            skLineSegment(sketch, "E20.0.1.5", {"start": v(-24, -38) * mm, "end": v(-17.07, -42) * mm});
            skLineSegment(sketch, "E20.0.2.0", {"start": v(-17.07, -70) * mm, "end": v(-17.07, -78) * mm});
            skLineSegment(sketch, "E20.0.2.1", {"start": v(-17.07, -78) * mm, "end": v(-24, -82) * mm});
            skLineSegment(sketch, "E20.0.2.2", {"start": v(-24, -82) * mm, "end": v(-30.93, -78) * mm});
            skLineSegment(sketch, "E20.0.2.3", {"start": v(-30.93, -78) * mm, "end": v(-30.93, -70) * mm});
            skLineSegment(sketch, "E20.0.2.4", {"start": v(-30.93, -70) * mm, "end": v(-24, -66) * mm});
            skLineSegment(sketch, "E20.0.2.5", {"start": v(-24, -66) * mm, "end": v(-17.07, -70) * mm});
            skLineSegment(sketch, "E20.1.0.0", {"start": v(-1.07, -14) * mm, "end": v(-1.07, -22) * mm});
            skLineSegment(sketch, "E20.1.0.1", {"start": v(-1.07, -22) * mm, "end": v(-8, -26) * mm});
            skLineSegment(sketch, "E20.1.0.2", {"start": v(-8, -26) * mm, "end": v(-14.93, -22) * mm});
            skLineSegment(sketch, "E20.1.0.3", {"start": v(-14.93, -22) * mm, "end": v(-14.93, -14) * mm});
            skLineSegment(sketch, "E20.1.0.4", {"start": v(-14.93, -14) * mm, "end": v(-8, -10) * mm});
            skLineSegment(sketch, "E20.1.0.5", {"start": v(-8, -10) * mm, "end": v(-1.07, -14) * mm});
            skLineSegment(sketch, "E20.1.1.0", {"start": v(-1.07, -42) * mm, "end": v(-1.07, -50) * mm});
            skLineSegment(sketch, "E20.1.1.1", {"start": v(-1.07, -50) * mm, "end": v(-8, -54) * mm});
            skLineSegment(sketch, "E20.1.1.2", {"start": v(-8, -54) * mm, "end": v(-14.93, -50) * mm});
            skLineSegment(sketch, "E20.1.1.3", {"start": v(-14.93, -50) * mm, "end": v(-14.93, -42) * mm});
            skLineSegment(sketch, "E20.1.1.4", {"start": v(-14.93, -42) * mm, "end": v(-8, -38) * mm});
            skLineSegment(sketch, "E20.1.1.5", {"start": v(-8, -38) * mm, "end": v(-1.07, -42) * mm});
            skLineSegment(sketch, "E20.1.2.0", {"start": v(-1.07, -70) * mm, "end": v(-1.07, -78) * mm});
            skLineSegment(sketch, "E20.1.2.1", {"start": v(-1.07, -78) * mm, "end": v(-8, -82) * mm});
            skLineSegment(sketch, "E20.1.2.2", {"start": v(-8, -82) * mm, "end": v(-14.93, -78) * mm});
            skLineSegment(sketch, "E20.1.2.3", {"start": v(-14.93, -78) * mm, "end": v(-14.93, -70) * mm});
            skLineSegment(sketch, "E20.1.2.4", {"start": v(-14.93, -70) * mm, "end": v(-8, -66) * mm});
            skLineSegment(sketch, "E20.1.2.5", {"start": v(-8, -66) * mm, "end": v(-1.07, -70) * mm});
            skLineSegment(sketch, "E20.2.0.0", {"start": v(14.93, -14) * mm, "end": v(14.93, -22) * mm});
            skLineSegment(sketch, "E20.2.0.1", {"start": v(14.93, -22) * mm, "end": v(8, -26) * mm});
            skLineSegment(sketch, "E20.2.0.2", {"start": v(8, -26) * mm, "end": v(1.07, -22) * mm});
            skLineSegment(sketch, "E20.2.0.3", {"start": v(1.07, -22) * mm, "end": v(1.07, -14) * mm});
            skLineSegment(sketch, "E20.2.0.4", {"start": v(1.07, -14) * mm, "end": v(8, -10) * mm});
            skLineSegment(sketch, "E20.2.0.5", {"start": v(8, -10) * mm, "end": v(14.93, -14) * mm});
            skLineSegment(sketch, "E20.2.1.0", {"start": v(14.93, -42) * mm, "end": v(14.93, -50) * mm});
            skLineSegment(sketch, "E20.2.1.1", {"start": v(14.93, -50) * mm, "end": v(8, -54) * mm});
            skLineSegment(sketch, "E20.2.1.2", {"start": v(8, -54) * mm, "end": v(1.07, -50) * mm});
            skLineSegment(sketch, "E20.2.1.3", {"start": v(1.07, -50) * mm, "end": v(1.07, -42) * mm});
            skLineSegment(sketch, "E20.2.1.4", {"start": v(1.07, -42) * mm, "end": v(8, -38) * mm});
            skLineSegment(sketch, "E20.2.1.5", {"start": v(8, -38) * mm, "end": v(14.93, -42) * mm});
            skLineSegment(sketch, "E20.2.2.0", {"start": v(14.93, -70) * mm, "end": v(14.93, -78) * mm});
            skLineSegment(sketch, "E20.2.2.1", {"start": v(14.93, -78) * mm, "end": v(8, -82) * mm});
            skLineSegment(sketch, "E20.2.2.2", {"start": v(8, -82) * mm, "end": v(1.07, -78) * mm});
            skLineSegment(sketch, "E20.2.2.3", {"start": v(1.07, -78) * mm, "end": v(1.07, -70) * mm});
            skLineSegment(sketch, "E20.2.2.4", {"start": v(1.07, -70) * mm, "end": v(8, -66) * mm});
            skLineSegment(sketch, "E20.2.2.5", {"start": v(8, -66) * mm, "end": v(14.93, -70) * mm});
            skLineSegment(sketch, "E20.3.0.0", {"start": v(30.93, -14) * mm, "end": v(30.93, -22) * mm});
            skLineSegment(sketch, "E20.3.0.1", {"start": v(30.93, -22) * mm, "end": v(24, -26) * mm});
            skLineSegment(sketch, "E20.3.0.2", {"start": v(24, -26) * mm, "end": v(17.07, -22) * mm});
            skLineSegment(sketch, "E20.3.0.3", {"start": v(17.07, -22) * mm, "end": v(17.07, -14) * mm});
            skLineSegment(sketch, "E20.3.0.4", {"start": v(17.07, -14) * mm, "end": v(24, -10) * mm});
            skLineSegment(sketch, "E20.3.0.5", {"start": v(24, -10) * mm, "end": v(30.93, -14) * mm});
            skLineSegment(sketch, "E20.3.1.0", {"start": v(30.93, -42) * mm, "end": v(30.93, -50) * mm});
            skLineSegment(sketch, "E20.3.1.1", {"start": v(30.93, -50) * mm, "end": v(24, -54) * mm});
            skLineSegment(sketch, "E20.3.1.2", {"start": v(24, -54) * mm, "end": v(17.07, -50) * mm});
            skLineSegment(sketch, "E20.3.1.3", {"start": v(17.07, -50) * mm, "end": v(17.07, -42) * mm});
            skLineSegment(sketch, "E20.3.1.4", {"start": v(17.07, -42) * mm, "end": v(24, -38) * mm});
            skLineSegment(sketch, "E20.3.1.5", {"start": v(24, -38) * mm, "end": v(30.93, -42) * mm});
            skLineSegment(sketch, "E20.3.2.0", {"start": v(30.93, -70) * mm, "end": v(30.93, -78) * mm});
            skLineSegment(sketch, "E20.3.2.1", {"start": v(30.93, -78) * mm, "end": v(24, -82) * mm});
            skLineSegment(sketch, "E20.3.2.2", {"start": v(24, -82) * mm, "end": v(17.07, -78) * mm});
            skLineSegment(sketch, "E20.3.2.3", {"start": v(17.07, -78) * mm, "end": v(17.07, -70) * mm});
            skLineSegment(sketch, "E20.3.2.4", {"start": v(17.07, -70) * mm, "end": v(24, -66) * mm});
            skLineSegment(sketch, "E20.3.2.5", {"start": v(24, -66) * mm, "end": v(30.93, -70) * mm});
            skLineSegment(sketch, "E20.direction1", {"start": v(-17.07, -22) * mm, "end": v(-1.07, -22) * mm, "construction": true});
            skLineSegment(sketch, "E20.direction2", {"start": v(-17.07, -22) * mm, "end": v(-17.07, -50) * mm, "construction": true});
            skSolve(sketch);
        }
        {
            var Q0;
            {var subQ3=sQuery(id+"F5.wireOp",EDGE,"E17.1");Q0=makeQuery(id+"F5.imprint","IMPRINT",FACE,{"disambiguationData":[TD([[makeQuery(id+"F5.imprint","IMPRINT",EDGE,{"derivedFrom":subQ3}),-1.0]])]});}
            var Q1;
            {var subQ1=sQuery(id+"F5.wireOp",EDGE,"E18.1.0.2");Q1=makeQuery(id+"F5.imprint","IMPRINT",FACE,{"disambiguationData":[TD([[makeQuery(id+"F5.imprint","IMPRINT",EDGE,{"derivedFrom":subQ1}),-1.0]])]});}
            var Q2;
            {var subQ1=sQuery(id+"F5.wireOp",EDGE,"E18.2.0.2");Q2=makeQuery(id+"F5.imprint","IMPRINT",FACE,{"disambiguationData":[TD([[makeQuery(id+"F5.imprint","IMPRINT",EDGE,{"derivedFrom":subQ1}),-1.0]])]});}
            var Q3;
            {var subQ1=sQuery(id+"F5.wireOp",EDGE,"E18.3.0.2");Q3=makeQuery(id+"F5.imprint","IMPRINT",FACE,{"disambiguationData":[TD([[makeQuery(id+"F5.imprint","IMPRINT",EDGE,{"derivedFrom":subQ1}),-1.0]])]});}
            var Q4;
            {var subQ3=sQuery(id+"F5.wireOp",EDGE,"E18.4.0.3");Q4=makeQuery(id+"F5.imprint","IMPRINT",FACE,{"disambiguationData":[TD([[makeQuery(id+"F5.imprint","IMPRINT",EDGE,{"derivedFrom":subQ3}),-1.0]])]});}
            var Q5;
            Q5=makeQuery(id+"F5.imprint","IMPRINT",FACE,{"disambiguationData":[TD([[makeQuery(id+"F5.imprint","IMPRINT",EDGE,{"derivedFrom":sQuery(id+"F5.wireOp",EDGE,"E20.3.0.0")}),-1.0]])]});
            var Q6;
            Q6=makeQuery(id+"F5.imprint","IMPRINT",FACE,{"disambiguationData":[TD([[makeQuery(id+"F5.imprint","IMPRINT",EDGE,{"derivedFrom":sQuery(id+"F5.wireOp",EDGE,"E20.2.0.0")}),-1.0]])]});
            var Q7;
            Q7=makeQuery(id+"F5.imprint","IMPRINT",FACE,{"disambiguationData":[TD([[makeQuery(id+"F5.imprint","IMPRINT",EDGE,{"derivedFrom":sQuery(id+"F5.wireOp",EDGE,"E20.1.0.0")}),-1.0]])]});
            var Q8;
            Q8=makeQuery(id+"F5.imprint","IMPRINT",FACE,{"disambiguationData":[TD([[makeQuery(id+"F5.imprint","IMPRINT",EDGE,{"derivedFrom":sQuery(id+"F5.wireOp",EDGE,"E19.0")}),-1.0]])]});
            var Q9;
            {var subQ2=sQuery(id+"F5.wireOp",EDGE,"E18.4.1.3");Q9=makeQuery(id+"F5.imprint","IMPRINT",FACE,{"disambiguationData":[TD([[makeQuery(id+"F5.imprint","IMPRINT",EDGE,{"derivedFrom":subQ2}),-1.0]])]});}
            var Q10;
            Q10=makeQuery(id+"F5.imprint","IMPRINT",FACE,{"disambiguationData":[TD([[makeQuery(id+"F5.imprint","IMPRINT",EDGE,{"derivedFrom":sQuery(id+"F5.wireOp",EDGE,"E18.3.1.0")}),-1.0]])]});
            var Q11;
            Q11=makeQuery(id+"F5.imprint","IMPRINT",FACE,{"disambiguationData":[TD([[makeQuery(id+"F5.imprint","IMPRINT",EDGE,{"derivedFrom":sQuery(id+"F5.wireOp",EDGE,"E18.2.1.0")}),-1.0]])]});
            var Q12;
            Q12=makeQuery(id+"F5.imprint","IMPRINT",FACE,{"disambiguationData":[TD([[makeQuery(id+"F5.imprint","IMPRINT",EDGE,{"derivedFrom":sQuery(id+"F5.wireOp",EDGE,"E18.1.1.0")}),-1.0]])]});
            var Q13;
            {var subQ0=sQuery(id+"F5.wireOp",EDGE,"E18.0.1.0");Q13=makeQuery(id+"F5.imprint","IMPRINT",FACE,{"disambiguationData":[TD([[makeQuery(id+"F5.imprint","IMPRINT",EDGE,{"derivedFrom":subQ0}),-1.0]])]});}
            var Q14;
            Q14=makeQuery(id+"F5.imprint","IMPRINT",FACE,{"disambiguationData":[TD([[makeQuery(id+"F5.imprint","IMPRINT",EDGE,{"derivedFrom":sQuery(id+"F5.wireOp",EDGE,"E20.0.1.0")}),-1.0]])]});
            var Q15;
            Q15=makeQuery(id+"F5.imprint","IMPRINT",FACE,{"disambiguationData":[TD([[makeQuery(id+"F5.imprint","IMPRINT",EDGE,{"derivedFrom":sQuery(id+"F5.wireOp",EDGE,"E20.1.1.0")}),-1.0]])]});
            var Q16;
            Q16=makeQuery(id+"F5.imprint","IMPRINT",FACE,{"disambiguationData":[TD([[makeQuery(id+"F5.imprint","IMPRINT",EDGE,{"derivedFrom":sQuery(id+"F5.wireOp",EDGE,"E20.2.1.0")}),-1.0]])]});
            var Q17;
            Q17=makeQuery(id+"F5.imprint","IMPRINT",FACE,{"disambiguationData":[TD([[makeQuery(id+"F5.imprint","IMPRINT",EDGE,{"derivedFrom":sQuery(id+"F5.wireOp",EDGE,"E20.3.1.0")}),-1.0]])]});
            var Q18;
            {var subQ2=sQuery(id+"F5.wireOp",EDGE,"E18.4.2.3");Q18=makeQuery(id+"F5.imprint","IMPRINT",FACE,{"disambiguationData":[TD([[makeQuery(id+"F5.imprint","IMPRINT",EDGE,{"derivedFrom":subQ2}),-1.0]])]});}
            var Q19;
            Q19=makeQuery(id+"F5.imprint","IMPRINT",FACE,{"disambiguationData":[TD([[makeQuery(id+"F5.imprint","IMPRINT",EDGE,{"derivedFrom":sQuery(id+"F5.wireOp",EDGE,"E18.3.2.0")}),-1.0]])]});
            var Q20;
            Q20=makeQuery(id+"F5.imprint","IMPRINT",FACE,{"disambiguationData":[TD([[makeQuery(id+"F5.imprint","IMPRINT",EDGE,{"derivedFrom":sQuery(id+"F5.wireOp",EDGE,"E18.2.2.0")}),-1.0]])]});
            var Q21;
            Q21=makeQuery(id+"F5.imprint","IMPRINT",FACE,{"disambiguationData":[TD([[makeQuery(id+"F5.imprint","IMPRINT",EDGE,{"derivedFrom":sQuery(id+"F5.wireOp",EDGE,"E18.1.2.0")}),-1.0]])]});
            var Q22;
            {var subQ0=sQuery(id+"F5.wireOp",EDGE,"E18.0.2.0");Q22=makeQuery(id+"F5.imprint","IMPRINT",FACE,{"disambiguationData":[TD([[makeQuery(id+"F5.imprint","IMPRINT",EDGE,{"derivedFrom":subQ0}),-1.0]])]});}
            var Q23;
            Q23=makeQuery(id+"F5.imprint","IMPRINT",FACE,{"disambiguationData":[TD([[makeQuery(id+"F5.imprint","IMPRINT",EDGE,{"derivedFrom":sQuery(id+"F5.wireOp",EDGE,"E20.0.2.0")}),-1.0]])]});
            var Q24;
            {var subQ0=sQuery(id+"F5.wireOp",EDGE,"E18.0.3.0");Q24=makeQuery(id+"F5.imprint","IMPRINT",FACE,{"disambiguationData":[TD([[makeQuery(id+"F5.imprint","IMPRINT",EDGE,{"derivedFrom":subQ0}),-1.0]])]});}
            var Q25;
            Q25=makeQuery(id+"F5.imprint","IMPRINT",FACE,{"disambiguationData":[TD([[makeQuery(id+"F5.imprint","IMPRINT",EDGE,{"derivedFrom":sQuery(id+"F5.wireOp",EDGE,"E18.1.3.0")}),-1.0]])]});
            var Q26;
            Q26=makeQuery(id+"F5.imprint","IMPRINT",FACE,{"disambiguationData":[TD([[makeQuery(id+"F5.imprint","IMPRINT",EDGE,{"derivedFrom":sQuery(id+"F5.wireOp",EDGE,"E20.1.2.0")}),-1.0]])]});
            var Q27;
            Q27=makeQuery(id+"F5.imprint","IMPRINT",FACE,{"disambiguationData":[TD([[makeQuery(id+"F5.imprint","IMPRINT",EDGE,{"derivedFrom":sQuery(id+"F5.wireOp",EDGE,"E18.2.3.0")}),-1.0]])]});
            var Q28;
            Q28=makeQuery(id+"F5.imprint","IMPRINT",FACE,{"disambiguationData":[TD([[makeQuery(id+"F5.imprint","IMPRINT",EDGE,{"derivedFrom":sQuery(id+"F5.wireOp",EDGE,"E20.2.2.0")}),-1.0]])]});
            var Q29;
            Q29=makeQuery(id+"F5.imprint","IMPRINT",FACE,{"disambiguationData":[TD([[makeQuery(id+"F5.imprint","IMPRINT",EDGE,{"derivedFrom":sQuery(id+"F5.wireOp",EDGE,"E18.3.3.0")}),-1.0]])]});
            var Q30;
            Q30=makeQuery(id+"F5.imprint","IMPRINT",FACE,{"disambiguationData":[TD([[makeQuery(id+"F5.imprint","IMPRINT",EDGE,{"derivedFrom":sQuery(id+"F5.wireOp",EDGE,"E20.3.2.0")}),-1.0]])]});
            var Q31;
            {var subQ0=sQuery(id+"F5.wireOp",EDGE,"E18.4.3.4");Q31=makeQuery(id+"F5.imprint","IMPRINT",FACE,{"disambiguationData":[TD([[makeQuery(id+"F5.imprint","IMPRINT",EDGE,{"derivedFrom":subQ0}),-1.0]])]});}
            extrude(context, id + "F6", {"entities" : qUnion([Q0, Q1, Q2, Q3, Q4, Q5, Q6, Q7, Q8, Q9, Q10, Q11, Q12, Q13, Q14, Q15, Q16, Q17, Q18, Q19, Q20, Q21, Q22, Q23, Q24, Q25, Q26, Q27, Q28, Q29, Q30, Q31]), "operationType" : NewBodyOperationType.REMOVE, "oppositeDirection" : true, "depth" : 2 * mm});
        }
        {
            var Q0;
            Q0=makeQuery(id+"F2.opExtrude","CAP_FACE",FACE,{"disambiguationData":[OSD([sQuery(id+"F0.wireOp",EDGE,"E0.left"),sQuery(id+"F0.wireOp",EDGE,"E1"),sQuery(id+"F0.wireOp",EDGE,"E2"),sQuery(id+"F0.wireOp",EDGE,"E3")])],"isStart":false});
            var sketch = newSketch(context, id + "F7", { "sketchPlane" : qUnion([Q0])});
            skLineSegment(sketch, "E21.bottom", {"start": v(-41, -25) * mm, "end": v(-31, -25) * mm});
            skLineSegment(sketch, "E21.top", {"start": v(-41, -50) * mm, "end": v(-31, -50) * mm});
            skLineSegment(sketch, "E21.left", {"start": v(-41, -25) * mm, "end": v(-41, -50) * mm});
            skLineSegment(sketch, "E21.right", {"start": v(-31, -25) * mm, "end": v(-31, -50) * mm});
            skLineSegment(sketch, "E22.MirrorCS", {"start": v(31, -25) * mm, "end": v(31, -50) * mm});
            skLineSegment(sketch, "E23.MirrorCS", {"start": v(41, -25) * mm, "end": v(41, -50) * mm});
            skLineSegment(sketch, "E24.MirrorCS", {"start": v(41, -25) * mm, "end": v(31, -25) * mm});
            skLineSegment(sketch, "E25.MirrorCS", {"start": v(41, -50) * mm, "end": v(31, -50) * mm});
            skArc(sketch, "E26", {"start": v(-41, -90.5) * mm, "mid": v(-36.75, -100.75) * mm, "end": v(-26.5, -105) * mm});
            skLineSegment(sketch, "E27", {"start": v(-26.5, -97) * mm, "end": v(-26.5, -105) * mm});
            skArc(sketch, "E28.MirrorCS", {"start": v(41, -90.5) * mm, "mid": v(36.75, -100.75) * mm, "end": v(26.5, -105) * mm});
            skLineSegment(sketch, "E29.MirrorCS", {"start": v(26.5, -97) * mm, "end": v(26.5, -105) * mm});
            skCircle(sketch, "E30", {"center": v(-38.5, -30) * mm, "radius": 1.23 * mm});
            skLineSegment(sketch, "E31", {"start": v(-41, -37.5) * mm, "end": v(-31, -37.5) * mm, "construction": true});
            skCircle(sketch, "E32.MirrorC", {"center": v(-38.5, -45) * mm, "radius": 1.23 * mm});
            skCircle(sketch, "E33.MirrorC", {"center": v(38.5, -30) * mm, "radius": 1.23 * mm});
            skCircle(sketch, "E34.MirrorC", {"center": v(38.5, -45) * mm, "radius": 1.23 * mm});
            skCircle(sketch, "E35", {"center": v(-38.24, -93) * mm, "radius": 1.23 * mm});
            skLineSegment(sketch, "E36", {"start": v(-41, -90.5) * mm, "end": v(-33, -90.5) * mm});
            skArc(sketch, "E37.0", {"start": v(-33, -90.5) * mm, "mid": v(-31.1, -95.1) * mm, "end": v(-26.5, -97) * mm});
            skLineSegment(sketch, "E38.MirrorCS", {"start": v(41, -90.5) * mm, "end": v(33, -90.5) * mm});
            skArc(sketch, "E39.MirrorCS", {"start": v(33, -90.5) * mm, "mid": v(31.1, -95.1) * mm, "end": v(26.5, -97) * mm});
            skArc(sketch, "E40.0", {"start": v(-38.5, -90.5) * mm, "mid": v(-34.99, -98.99) * mm, "end": v(-26.5, -102.5) * mm, "construction": true});
            skLineSegment(sketch, "E41", {"start": v(-26.5, -90.5) * mm, "end": v(-30.04, -94.04) * mm, "construction": true});
            skCircle(sketch, "E42.MirrorC", {"center": v(-29, -102.24) * mm, "radius": 1.23 * mm});
            skCircle(sketch, "E43.MirrorC", {"center": v(38.24, -93) * mm, "radius": 1.23 * mm});
            skCircle(sketch, "E44.MirrorC", {"center": v(29, -102.24) * mm, "radius": 1.23 * mm});
            skSolve(sketch);
        }
        {
            var Q0;
            Q0=makeQuery(id+"F7.imprint","IMPRINT",FACE,{"disambiguationData":[TD([[makeQuery(id+"F7.imprint","IMPRINT",EDGE,{"derivedFrom":sQuery(id+"F7.wireOp",EDGE,"E26")}),1.0]])]});
            var Q1;
            {var subQ2=sQuery(id+"F7.wireOp",EDGE,"E21.right");Q1=makeQuery(id+"F7.imprint","IMPRINT",FACE,{"disambiguationData":[TD([[makeQuery(id+"F7.imprint","IMPRINT",EDGE,{"derivedFrom":subQ2}),-1.0]])]});}
            var Q2;
            Q2=makeQuery(id+"F7.imprint","IMPRINT",FACE,{"disambiguationData":[TD([[makeQuery(id+"F7.imprint","IMPRINT",EDGE,{"derivedFrom":sQuery(id+"F7.wireOp",EDGE,"E28.MirrorCS")}),-1.0]])]});
            var Q3;
            Q3=makeQuery(id+"F7.imprint","IMPRINT",FACE,{"disambiguationData":[TD([[makeQuery(id+"F7.imprint","IMPRINT",EDGE,{"derivedFrom":sQuery(id+"F7.wireOp",EDGE,"E22.MirrorCS")}),1.0]])]});
            var Q4;
            Q4=makeQuery(id+"F7.imprint","IMPRINT",FACE,{"disambiguationData":[TD([[makeQuery(id+"F7.imprint","IMPRINT",EDGE,{"derivedFrom":sQuery(id+"F7.wireOp",EDGE,"E30")}),-1.0]])]});
            extrude(context, id + "F8", {"entities" : qUnion([Q0, Q1, Q2, Q3, Q4]), "depth" : 2 * mm});
        }
        {
            var Q0;
            Q0=makeQuery(id+"F6.boolean.opBoolean","COPY",EDGE,{"derivedFrom":makeQuery(id+"F6.opExtrude","CAP_EDGE",EDGE,{"disambiguationData":[OSD([sQuery(id+"F5.wireOp",EDGE,"E20.1.0.5")])],"isStart":true})});
            var Q1;
            Q1=makeQuery(id+"F6.boolean.opBoolean","COPY",EDGE,{"derivedFrom":makeQuery(id+"F6.opExtrude","CAP_EDGE",EDGE,{"disambiguationData":[OSD([sQuery(id+"F5.wireOp",EDGE,"E20.1.0.0")])],"isStart":true})});
            var Q2;
            Q2=makeQuery(id+"F6.boolean.opBoolean","COPY",EDGE,{"derivedFrom":makeQuery(id+"F6.opExtrude","CAP_EDGE",EDGE,{"disambiguationData":[OSD([sQuery(id+"F5.wireOp",EDGE,"E20.1.0.4")])],"isStart":true})});
            var Q3;
            Q3=makeQuery(id+"F6.boolean.opBoolean","COPY",EDGE,{"derivedFrom":makeQuery(id+"F6.opExtrude","CAP_EDGE",EDGE,{"disambiguationData":[OSD([sQuery(id+"F5.wireOp",EDGE,"E20.1.0.5")])],"isStart":false})});
            var Q4;
            Q4=makeQuery(id+"F6.boolean.opBoolean","COPY",EDGE,{"derivedFrom":makeQuery(id+"F6.opExtrude","CAP_EDGE",EDGE,{"disambiguationData":[OSD([sQuery(id+"F5.wireOp",EDGE,"E20.1.0.4")])],"isStart":false})});
            var Q5;
            Q5=makeQuery(id+"F6.boolean.opBoolean","COPY",EDGE,{"derivedFrom":makeQuery(id+"F6.opExtrude","CAP_EDGE",EDGE,{"disambiguationData":[OSD([sQuery(id+"F5.wireOp",EDGE,"E20.1.0.0")])],"isStart":false})});
            var Q6;
            {var subQ0=sQuery(id+"F5.wireOp",EDGE,"E16.3");Q6=makeQuery(id+"F6.boolean.opBoolean","COPY",EDGE,{"derivedFrom":makeQuery(id+"F6.opExtrude","CAP_EDGE",EDGE,{"disambiguationData":[OSD([subQ0]),TDD([makeQuery(id+"F5.imprint","IMPRINT",EDGE,{"disambiguationData":[TD([[makeQuery(id+"F5.imprint","INTERSECT",VERTEX,{"derivedFrom":[sQuery(id+"F5.wireOp",EDGE,"E16.0"),subQ0]}),-1.0]])],"derivedFrom":subQ0})])],"isStart":false})});}
            var Q7;
            Q7=makeQuery(id+"F6.boolean.opBoolean","COPY",EDGE,{"derivedFrom":makeQuery(id+"F6.opExtrude","CAP_EDGE",EDGE,{"disambiguationData":[OSD([sQuery(id+"F5.wireOp",EDGE,"E17.0")])],"isStart":false})});
            var Q8;
            Q8=makeQuery(id+"F6.boolean.opBoolean","COPY",FACE,{"derivedFrom":makeQuery(id+"F6.opExtrude","CAP_FACE",FACE,{"disambiguationData":[OSD([sQuery(id+"F5.wireOp",EDGE,"E16.0"),sQuery(id+"F5.wireOp",EDGE,"E16.3"),sQuery(id+"F5.wireOp",EDGE,"E17.0"),sQuery(id+"F5.wireOp",EDGE,"E17.1")])],"isStart":false})});
            var Q9;
            Q9=makeQuery(id+"F6.boolean.opBoolean","COPY",FACE,{"derivedFrom":makeQuery(id+"F6.opExtrude","CAP_FACE",FACE,{"disambiguationData":[OSD([sQuery(id+"F5.wireOp",EDGE,"E20.2.0.0"),sQuery(id+"F5.wireOp",EDGE,"E20.2.0.1"),sQuery(id+"F5.wireOp",EDGE,"E20.2.0.2"),sQuery(id+"F5.wireOp",EDGE,"E20.2.0.3"),sQuery(id+"F5.wireOp",EDGE,"E20.2.0.4"),sQuery(id+"F5.wireOp",EDGE,"E20.2.0.5")])],"isStart":false})});
            var Q10;
            Q10=makeQuery(id+"F6.boolean.opBoolean","COPY",FACE,{"derivedFrom":makeQuery(id+"F6.opExtrude","CAP_FACE",FACE,{"disambiguationData":[OSD([sQuery(id+"F5.wireOp",EDGE,"E20.1.0.0"),sQuery(id+"F5.wireOp",EDGE,"E20.1.0.1"),sQuery(id+"F5.wireOp",EDGE,"E20.1.0.2"),sQuery(id+"F5.wireOp",EDGE,"E20.1.0.3"),sQuery(id+"F5.wireOp",EDGE,"E20.1.0.4"),sQuery(id+"F5.wireOp",EDGE,"E20.1.0.5")])],"isStart":false})});
            var Q11;
            Q11=makeQuery(id+"F6.boolean.opBoolean","COPY",FACE,{"derivedFrom":makeQuery(id+"F6.opExtrude","CAP_FACE",FACE,{"disambiguationData":[OSD([sQuery(id+"F5.wireOp",EDGE,"E16.3"),sQuery(id+"F5.wireOp",EDGE,"E18.2.0.1"),sQuery(id+"F5.wireOp",EDGE,"E18.2.0.2"),sQuery(id+"F5.wireOp",EDGE,"E18.2.0.3"),sQuery(id+"F5.wireOp",EDGE,"E18.2.0.4")])],"isStart":false})});
            var Q12;
            Q12=makeQuery(id+"F6.boolean.opBoolean","COPY",FACE,{"derivedFrom":makeQuery(id+"F6.opExtrude","CAP_FACE",FACE,{"disambiguationData":[OSD([sQuery(id+"F5.wireOp",EDGE,"E16.3"),sQuery(id+"F5.wireOp",EDGE,"E18.1.0.1"),sQuery(id+"F5.wireOp",EDGE,"E18.1.0.2"),sQuery(id+"F5.wireOp",EDGE,"E18.1.0.3"),sQuery(id+"F5.wireOp",EDGE,"E18.1.0.4")])],"isStart":false})});
            var Q13;
            Q13=makeQuery(id+"F6.boolean.opBoolean","COPY",FACE,{"derivedFrom":makeQuery(id+"F6.opExtrude","CAP_FACE",FACE,{"disambiguationData":[OSD([sQuery(id+"F5.wireOp",EDGE,"E19.0"),sQuery(id+"F5.wireOp",EDGE,"E19.1"),sQuery(id+"F5.wireOp",EDGE,"E19.2"),sQuery(id+"F5.wireOp",EDGE,"E19.3"),sQuery(id+"F5.wireOp",EDGE,"E19.4"),sQuery(id+"F5.wireOp",EDGE,"E19.5")])],"isStart":false})});
            var Q14;
            Q14=makeQuery(id+"F6.boolean.opBoolean","COPY",FACE,{"derivedFrom":makeQuery(id+"F6.opExtrude","CAP_FACE",FACE,{"disambiguationData":[OSD([sQuery(id+"F5.wireOp",EDGE,"E18.1.1.0"),sQuery(id+"F5.wireOp",EDGE,"E18.1.1.1"),sQuery(id+"F5.wireOp",EDGE,"E18.1.1.2"),sQuery(id+"F5.wireOp",EDGE,"E18.1.1.3"),sQuery(id+"F5.wireOp",EDGE,"E18.1.1.4"),sQuery(id+"F5.wireOp",EDGE,"E18.1.1.5")])],"isStart":false})});
            var Q15;
            Q15=makeQuery(id+"F6.boolean.opBoolean","COPY",FACE,{"derivedFrom":makeQuery(id+"F6.opExtrude","CAP_FACE",FACE,{"disambiguationData":[OSD([sQuery(id+"F5.wireOp",EDGE,"E20.3.0.0"),sQuery(id+"F5.wireOp",EDGE,"E20.3.0.1"),sQuery(id+"F5.wireOp",EDGE,"E20.3.0.2"),sQuery(id+"F5.wireOp",EDGE,"E20.3.0.3"),sQuery(id+"F5.wireOp",EDGE,"E20.3.0.4"),sQuery(id+"F5.wireOp",EDGE,"E20.3.0.5")])],"isStart":false})});
            var Q16;
            Q16=makeQuery(id+"F6.boolean.opBoolean","COPY",FACE,{"derivedFrom":makeQuery(id+"F6.opExtrude","CAP_FACE",FACE,{"disambiguationData":[OSD([sQuery(id+"F5.wireOp",EDGE,"E16.1"),sQuery(id+"F5.wireOp",EDGE,"E16.3"),sQuery(id+"F5.wireOp",EDGE,"E18.4.0.3"),sQuery(id+"F5.wireOp",EDGE,"E18.4.0.4")])],"isStart":false})});
            var Q17;
            Q17=makeQuery(id+"F6.boolean.opBoolean","COPY",FACE,{"derivedFrom":makeQuery(id+"F6.opExtrude","CAP_FACE",FACE,{"disambiguationData":[OSD([sQuery(id+"F5.wireOp",EDGE,"E16.3"),sQuery(id+"F5.wireOp",EDGE,"E18.3.0.1"),sQuery(id+"F5.wireOp",EDGE,"E18.3.0.2"),sQuery(id+"F5.wireOp",EDGE,"E18.3.0.3"),sQuery(id+"F5.wireOp",EDGE,"E18.3.0.4")])],"isStart":false})});
            var Q18;
            Q18=makeQuery(id+"F6.boolean.opBoolean","COPY",FACE,{"derivedFrom":makeQuery(id+"F6.opExtrude","CAP_FACE",FACE,{"disambiguationData":[OSD([sQuery(id+"F5.wireOp",EDGE,"E16.1"),sQuery(id+"F5.wireOp",EDGE,"E18.4.1.3"),sQuery(id+"F5.wireOp",EDGE,"E18.4.1.4"),sQuery(id+"F5.wireOp",EDGE,"E18.4.1.5")])],"isStart":false})});
            var Q19;
            Q19=makeQuery(id+"F6.boolean.opBoolean","COPY",FACE,{"derivedFrom":makeQuery(id+"F6.opExtrude","CAP_FACE",FACE,{"disambiguationData":[OSD([sQuery(id+"F5.wireOp",EDGE,"E18.3.1.0"),sQuery(id+"F5.wireOp",EDGE,"E18.3.1.1"),sQuery(id+"F5.wireOp",EDGE,"E18.3.1.2"),sQuery(id+"F5.wireOp",EDGE,"E18.3.1.3"),sQuery(id+"F5.wireOp",EDGE,"E18.3.1.4"),sQuery(id+"F5.wireOp",EDGE,"E18.3.1.5")])],"isStart":false})});
            var Q20;
            Q20=makeQuery(id+"F6.boolean.opBoolean","COPY",FACE,{"derivedFrom":makeQuery(id+"F6.opExtrude","CAP_FACE",FACE,{"disambiguationData":[OSD([sQuery(id+"F5.wireOp",EDGE,"E18.2.1.0"),sQuery(id+"F5.wireOp",EDGE,"E18.2.1.1"),sQuery(id+"F5.wireOp",EDGE,"E18.2.1.2"),sQuery(id+"F5.wireOp",EDGE,"E18.2.1.3"),sQuery(id+"F5.wireOp",EDGE,"E18.2.1.4"),sQuery(id+"F5.wireOp",EDGE,"E18.2.1.5")])],"isStart":false})});
            var Q21;
            Q21=makeQuery(id+"F6.boolean.opBoolean","COPY",FACE,{"derivedFrom":makeQuery(id+"F6.opExtrude","CAP_FACE",FACE,{"disambiguationData":[OSD([sQuery(id+"F5.wireOp",EDGE,"E20.0.1.0"),sQuery(id+"F5.wireOp",EDGE,"E20.0.1.1"),sQuery(id+"F5.wireOp",EDGE,"E20.0.1.2"),sQuery(id+"F5.wireOp",EDGE,"E20.0.1.3"),sQuery(id+"F5.wireOp",EDGE,"E20.0.1.4"),sQuery(id+"F5.wireOp",EDGE,"E20.0.1.5")])],"isStart":false})});
            var Q22;
            Q22=makeQuery(id+"F6.boolean.opBoolean","COPY",FACE,{"derivedFrom":makeQuery(id+"F6.opExtrude","CAP_FACE",FACE,{"disambiguationData":[OSD([sQuery(id+"F5.wireOp",EDGE,"E20.1.1.0"),sQuery(id+"F5.wireOp",EDGE,"E20.1.1.1"),sQuery(id+"F5.wireOp",EDGE,"E20.1.1.2"),sQuery(id+"F5.wireOp",EDGE,"E20.1.1.3"),sQuery(id+"F5.wireOp",EDGE,"E20.1.1.4"),sQuery(id+"F5.wireOp",EDGE,"E20.1.1.5")])],"isStart":false})});
            var Q23;
            Q23=makeQuery(id+"F6.boolean.opBoolean","COPY",FACE,{"derivedFrom":makeQuery(id+"F6.opExtrude","CAP_FACE",FACE,{"disambiguationData":[OSD([sQuery(id+"F5.wireOp",EDGE,"E20.2.1.0"),sQuery(id+"F5.wireOp",EDGE,"E20.2.1.1"),sQuery(id+"F5.wireOp",EDGE,"E20.2.1.2"),sQuery(id+"F5.wireOp",EDGE,"E20.2.1.3"),sQuery(id+"F5.wireOp",EDGE,"E20.2.1.4"),sQuery(id+"F5.wireOp",EDGE,"E20.2.1.5")])],"isStart":false})});
            var Q24;
            Q24=makeQuery(id+"F6.boolean.opBoolean","COPY",FACE,{"derivedFrom":makeQuery(id+"F6.opExtrude","CAP_FACE",FACE,{"disambiguationData":[OSD([sQuery(id+"F5.wireOp",EDGE,"E20.3.1.0"),sQuery(id+"F5.wireOp",EDGE,"E20.3.1.1"),sQuery(id+"F5.wireOp",EDGE,"E20.3.1.2"),sQuery(id+"F5.wireOp",EDGE,"E20.3.1.3"),sQuery(id+"F5.wireOp",EDGE,"E20.3.1.4"),sQuery(id+"F5.wireOp",EDGE,"E20.3.1.5")])],"isStart":false})});
            var Q25;
            Q25=makeQuery(id+"F6.boolean.opBoolean","COPY",FACE,{"derivedFrom":makeQuery(id+"F6.opExtrude","CAP_FACE",FACE,{"disambiguationData":[OSD([sQuery(id+"F5.wireOp",EDGE,"E18.3.2.0"),sQuery(id+"F5.wireOp",EDGE,"E18.3.2.1"),sQuery(id+"F5.wireOp",EDGE,"E18.3.2.2"),sQuery(id+"F5.wireOp",EDGE,"E18.3.2.3"),sQuery(id+"F5.wireOp",EDGE,"E18.3.2.4"),sQuery(id+"F5.wireOp",EDGE,"E18.3.2.5")])],"isStart":false})});
            var Q26;
            Q26=makeQuery(id+"F6.boolean.opBoolean","COPY",FACE,{"derivedFrom":makeQuery(id+"F6.opExtrude","CAP_FACE",FACE,{"disambiguationData":[OSD([sQuery(id+"F5.wireOp",EDGE,"E16.1"),sQuery(id+"F5.wireOp",EDGE,"E18.4.2.3"),sQuery(id+"F5.wireOp",EDGE,"E18.4.2.4"),sQuery(id+"F5.wireOp",EDGE,"E18.4.2.5")])],"isStart":false})});
            var Q27;
            Q27=makeQuery(id+"F6.boolean.opBoolean","COPY",FACE,{"derivedFrom":makeQuery(id+"F6.opExtrude","CAP_FACE",FACE,{"disambiguationData":[OSD([sQuery(id+"F5.wireOp",EDGE,"E18.2.2.0"),sQuery(id+"F5.wireOp",EDGE,"E18.2.2.1"),sQuery(id+"F5.wireOp",EDGE,"E18.2.2.2"),sQuery(id+"F5.wireOp",EDGE,"E18.2.2.3"),sQuery(id+"F5.wireOp",EDGE,"E18.2.2.4"),sQuery(id+"F5.wireOp",EDGE,"E18.2.2.5")])],"isStart":false})});
            var Q28;
            Q28=makeQuery(id+"F6.boolean.opBoolean","COPY",FACE,{"derivedFrom":makeQuery(id+"F6.opExtrude","CAP_FACE",FACE,{"disambiguationData":[OSD([sQuery(id+"F5.wireOp",EDGE,"E18.1.2.0"),sQuery(id+"F5.wireOp",EDGE,"E18.1.2.1"),sQuery(id+"F5.wireOp",EDGE,"E18.1.2.2"),sQuery(id+"F5.wireOp",EDGE,"E18.1.2.3"),sQuery(id+"F5.wireOp",EDGE,"E18.1.2.4"),sQuery(id+"F5.wireOp",EDGE,"E18.1.2.5")])],"isStart":false})});
            var Q29;
            Q29=makeQuery(id+"F6.boolean.opBoolean","COPY",FACE,{"derivedFrom":makeQuery(id+"F6.opExtrude","CAP_FACE",FACE,{"disambiguationData":[OSD([sQuery(id+"F5.wireOp",EDGE,"E16.0"),sQuery(id+"F5.wireOp",EDGE,"E18.0.2.0"),sQuery(id+"F5.wireOp",EDGE,"E18.0.2.1"),sQuery(id+"F5.wireOp",EDGE,"E18.0.2.2")])],"isStart":false})});
            var Q30;
            {var subQ0=sQuery(id+"F5.wireOp",EDGE,"E16.3");Q30=makeQuery(id+"F6.boolean.opBoolean","COPY",EDGE,{"derivedFrom":makeQuery(id+"F6.opExtrude","CAP_EDGE",EDGE,{"disambiguationData":[OSD([subQ0]),TDD([makeQuery(id+"F5.imprint","IMPRINT",EDGE,{"disambiguationData":[TD([[makeQuery(id+"F5.imprint","INTERSECT",VERTEX,{"derivedFrom":[sQuery(id+"F5.wireOp",EDGE,"E16.0"),subQ0]}),-1.0]])],"derivedFrom":subQ0})])],"isStart":true})});}
            var Q31;
            {var subQ0=sQuery(id+"F5.wireOp",EDGE,"E16.0");Q31=makeQuery(id+"F6.boolean.opBoolean","COPY",EDGE,{"derivedFrom":makeQuery(id+"F6.opExtrude","CAP_EDGE",EDGE,{"disambiguationData":[OSD([subQ0]),TDD([makeQuery(id+"F5.imprint","IMPRINT",EDGE,{"disambiguationData":[TD([[makeQuery(id+"F5.imprint","INTERSECT",VERTEX,{"derivedFrom":[subQ0,sQuery(id+"F5.wireOp",EDGE,"E16.3")]}),-1.0]])],"derivedFrom":subQ0})])],"isStart":true})});}
            var Q32;
            Q32=makeQuery(id+"F6.boolean.opBoolean","COPY",EDGE,{"derivedFrom":makeQuery(id+"F6.opExtrude","CAP_EDGE",EDGE,{"disambiguationData":[OSD([sQuery(id+"F5.wireOp",EDGE,"E17.1")])],"isStart":true})});
            var Q33;
            Q33=makeQuery(id+"F6.boolean.opBoolean","COPY",EDGE,{"derivedFrom":makeQuery(id+"F6.opExtrude","CAP_EDGE",EDGE,{"disambiguationData":[OSD([sQuery(id+"F5.wireOp",EDGE,"E17.0")])],"isStart":true})});
            var Q34;
            Q34=makeQuery(id+"F6.boolean.opBoolean","COPY",EDGE,{"derivedFrom":makeQuery(id+"F6.opExtrude","CAP_EDGE",EDGE,{"disambiguationData":[OSD([sQuery(id+"F5.wireOp",EDGE,"E18.1.0.4")])],"isStart":true})});
            var Q35;
            {var subQ0=sQuery(id+"F5.wireOp",EDGE,"E16.3");Q35=makeQuery(id+"F6.boolean.opBoolean","COPY",EDGE,{"derivedFrom":makeQuery(id+"F6.opExtrude","CAP_EDGE",EDGE,{"disambiguationData":[OSD([subQ0]),TDD([makeQuery(id+"F5.imprint","IMPRINT",EDGE,{"disambiguationData":[TD([[makeQuery(id+"F5.imprint","INTERSECT",VERTEX,{"derivedFrom":[subQ0,sQuery(id+"F5.wireOp",EDGE,"E18.1.0.4")]}),-1.0]])],"derivedFrom":subQ0})])],"isStart":true})});}
            var Q36;
            {var subQ0=sQuery(id+"F5.wireOp",EDGE,"E16.3");Q36=makeQuery(id+"F6.boolean.opBoolean","COPY",EDGE,{"derivedFrom":makeQuery(id+"F6.opExtrude","CAP_EDGE",EDGE,{"disambiguationData":[OSD([subQ0]),TDD([makeQuery(id+"F5.imprint","IMPRINT",EDGE,{"disambiguationData":[TD([[makeQuery(id+"F5.imprint","INTERSECT",VERTEX,{"derivedFrom":[subQ0,sQuery(id+"F5.wireOp",EDGE,"E18.2.0.4")]}),-1.0]])],"derivedFrom":subQ0})])],"isStart":true})});}
            var Q37;
            {var subQ0=sQuery(id+"F5.wireOp",EDGE,"E16.3");Q37=makeQuery(id+"F6.boolean.opBoolean","COPY",EDGE,{"derivedFrom":makeQuery(id+"F6.opExtrude","CAP_EDGE",EDGE,{"disambiguationData":[OSD([subQ0]),TDD([makeQuery(id+"F5.imprint","IMPRINT",EDGE,{"disambiguationData":[TD([[makeQuery(id+"F5.imprint","INTERSECT",VERTEX,{"derivedFrom":[subQ0,sQuery(id+"F5.wireOp",EDGE,"E18.3.0.4")]}),-1.0]])],"derivedFrom":subQ0})])],"isStart":true})});}
            var Q38;
            {var subQ0=sQuery(id+"F5.wireOp",EDGE,"E16.3");Q38=makeQuery(id+"F6.boolean.opBoolean","COPY",EDGE,{"derivedFrom":makeQuery(id+"F6.opExtrude","CAP_EDGE",EDGE,{"disambiguationData":[OSD([subQ0]),TDD([makeQuery(id+"F5.imprint","IMPRINT",EDGE,{"disambiguationData":[TD([[makeQuery(id+"F5.imprint","INTERSECT",VERTEX,{"derivedFrom":[sQuery(id+"F5.wireOp",EDGE,"E16.1"),subQ0]}),1.0]])],"derivedFrom":subQ0})])],"isStart":true})});}
            var Q39;
            {var subQ0=sQuery(id+"F5.wireOp",EDGE,"E16.1");Q39=makeQuery(id+"F6.boolean.opBoolean","COPY",EDGE,{"derivedFrom":makeQuery(id+"F6.opExtrude","CAP_EDGE",EDGE,{"disambiguationData":[OSD([subQ0]),TDD([makeQuery(id+"F5.imprint","IMPRINT",EDGE,{"disambiguationData":[TD([[makeQuery(id+"F5.imprint","INTERSECT",VERTEX,{"derivedFrom":[subQ0,sQuery(id+"F5.wireOp",EDGE,"E16.3")]}),-1.0]])],"derivedFrom":subQ0})])],"isStart":true})});}
            var Q40;
            Q40=makeQuery(id+"F6.boolean.opBoolean","COPY",EDGE,{"derivedFrom":makeQuery(id+"F6.opExtrude","CAP_EDGE",EDGE,{"disambiguationData":[OSD([sQuery(id+"F5.wireOp",EDGE,"E18.4.0.3")])],"isStart":true})});
            var Q41;
            Q41=makeQuery(id+"F6.boolean.opBoolean","COPY",EDGE,{"derivedFrom":makeQuery(id+"F6.opExtrude","CAP_EDGE",EDGE,{"disambiguationData":[OSD([sQuery(id+"F5.wireOp",EDGE,"E18.4.0.4")])],"isStart":true})});
            var Q42;
            Q42=makeQuery(id+"F6.boolean.opBoolean","COPY",EDGE,{"derivedFrom":makeQuery(id+"F6.opExtrude","CAP_EDGE",EDGE,{"disambiguationData":[OSD([sQuery(id+"F5.wireOp",EDGE,"E18.3.0.2")])],"isStart":true})});
            var Q43;
            Q43=makeQuery(id+"F6.boolean.opBoolean","COPY",EDGE,{"derivedFrom":makeQuery(id+"F6.opExtrude","CAP_EDGE",EDGE,{"disambiguationData":[OSD([sQuery(id+"F5.wireOp",EDGE,"E18.3.0.1")])],"isStart":true})});
            var Q44;
            Q44=makeQuery(id+"F6.boolean.opBoolean","COPY",EDGE,{"derivedFrom":makeQuery(id+"F6.opExtrude","CAP_EDGE",EDGE,{"disambiguationData":[OSD([sQuery(id+"F5.wireOp",EDGE,"E18.3.0.3")])],"isStart":true})});
            var Q45;
            Q45=makeQuery(id+"F6.boolean.opBoolean","COPY",EDGE,{"derivedFrom":makeQuery(id+"F6.opExtrude","CAP_EDGE",EDGE,{"disambiguationData":[OSD([sQuery(id+"F5.wireOp",EDGE,"E18.3.0.4")])],"isStart":true})});
            var Q46;
            Q46=makeQuery(id+"F6.boolean.opBoolean","COPY",EDGE,{"derivedFrom":makeQuery(id+"F6.opExtrude","CAP_EDGE",EDGE,{"disambiguationData":[OSD([sQuery(id+"F5.wireOp",EDGE,"E18.2.0.1")])],"isStart":true})});
            var Q47;
            Q47=makeQuery(id+"F6.boolean.opBoolean","COPY",EDGE,{"derivedFrom":makeQuery(id+"F6.opExtrude","CAP_EDGE",EDGE,{"disambiguationData":[OSD([sQuery(id+"F5.wireOp",EDGE,"E18.1.0.1")])],"isStart":true})});
            var Q48;
            Q48=makeQuery(id+"F6.boolean.opBoolean","COPY",EDGE,{"derivedFrom":makeQuery(id+"F6.opExtrude","CAP_EDGE",EDGE,{"disambiguationData":[OSD([sQuery(id+"F5.wireOp",EDGE,"E18.2.0.4")])],"isStart":true})});
            var Q49;
            Q49=makeQuery(id+"F6.boolean.opBoolean","COPY",EDGE,{"derivedFrom":makeQuery(id+"F6.opExtrude","CAP_EDGE",EDGE,{"disambiguationData":[OSD([sQuery(id+"F5.wireOp",EDGE,"E18.2.0.2")])],"isStart":true})});
            var Q50;
            Q50=makeQuery(id+"F6.boolean.opBoolean","COPY",EDGE,{"derivedFrom":makeQuery(id+"F6.opExtrude","CAP_EDGE",EDGE,{"disambiguationData":[OSD([sQuery(id+"F5.wireOp",EDGE,"E18.2.0.3")])],"isStart":true})});
            var Q51;
            Q51=makeQuery(id+"F6.boolean.opBoolean","COPY",EDGE,{"derivedFrom":makeQuery(id+"F6.opExtrude","CAP_EDGE",EDGE,{"disambiguationData":[OSD([sQuery(id+"F5.wireOp",EDGE,"E18.1.0.2")])],"isStart":true})});
            var Q52;
            Q52=makeQuery(id+"F6.boolean.opBoolean","COPY",EDGE,{"derivedFrom":makeQuery(id+"F6.opExtrude","CAP_EDGE",EDGE,{"disambiguationData":[OSD([sQuery(id+"F5.wireOp",EDGE,"E18.1.0.3")])],"isStart":true})});
            var Q53;
            Q53=makeQuery(id+"F6.boolean.opBoolean","COPY",EDGE,{"derivedFrom":makeQuery(id+"F6.opExtrude","CAP_EDGE",EDGE,{"disambiguationData":[OSD([sQuery(id+"F5.wireOp",EDGE,"E19.3")])],"isStart":true})});
            var Q54;
            Q54=makeQuery(id+"F6.boolean.opBoolean","COPY",EDGE,{"derivedFrom":makeQuery(id+"F6.opExtrude","CAP_EDGE",EDGE,{"disambiguationData":[OSD([sQuery(id+"F5.wireOp",EDGE,"E19.4")])],"isStart":true})});
            var Q55;
            Q55=makeQuery(id+"F6.boolean.opBoolean","COPY",EDGE,{"derivedFrom":makeQuery(id+"F6.opExtrude","CAP_EDGE",EDGE,{"disambiguationData":[OSD([sQuery(id+"F5.wireOp",EDGE,"E19.5")])],"isStart":true})});
            var Q56;
            Q56=makeQuery(id+"F6.boolean.opBoolean","COPY",EDGE,{"derivedFrom":makeQuery(id+"F6.opExtrude","CAP_EDGE",EDGE,{"disambiguationData":[OSD([sQuery(id+"F5.wireOp",EDGE,"E20.1.0.3")])],"isStart":true})});
            var Q57;
            Q57=makeQuery(id+"F6.boolean.opBoolean","COPY",EDGE,{"derivedFrom":makeQuery(id+"F6.opExtrude","CAP_EDGE",EDGE,{"disambiguationData":[OSD([sQuery(id+"F5.wireOp",EDGE,"E20.2.0.3")])],"isStart":true})});
            var Q58;
            Q58=makeQuery(id+"F6.boolean.opBoolean","COPY",EDGE,{"derivedFrom":makeQuery(id+"F6.opExtrude","CAP_EDGE",EDGE,{"disambiguationData":[OSD([sQuery(id+"F5.wireOp",EDGE,"E20.2.0.0")])],"isStart":true})});
            var Q59;
            Q59=makeQuery(id+"F6.boolean.opBoolean","COPY",EDGE,{"derivedFrom":makeQuery(id+"F6.opExtrude","CAP_EDGE",EDGE,{"disambiguationData":[OSD([sQuery(id+"F5.wireOp",EDGE,"E20.3.0.3")])],"isStart":true})});
            var Q60;
            Q60=makeQuery(id+"F6.boolean.opBoolean","COPY",EDGE,{"derivedFrom":makeQuery(id+"F6.opExtrude","CAP_EDGE",EDGE,{"disambiguationData":[OSD([sQuery(id+"F5.wireOp",EDGE,"E20.3.0.4")])],"isStart":true})});
            var Q61;
            Q61=makeQuery(id+"F6.boolean.opBoolean","COPY",EDGE,{"derivedFrom":makeQuery(id+"F6.opExtrude","CAP_EDGE",EDGE,{"disambiguationData":[OSD([sQuery(id+"F5.wireOp",EDGE,"E20.3.0.5")])],"isStart":true})});
            var Q62;
            Q62=makeQuery(id+"F6.boolean.opBoolean","COPY",EDGE,{"derivedFrom":makeQuery(id+"F6.opExtrude","CAP_EDGE",EDGE,{"disambiguationData":[OSD([sQuery(id+"F5.wireOp",EDGE,"E20.3.0.0")])],"isStart":true})});
            var Q63;
            Q63=makeQuery(id+"F6.boolean.opBoolean","COPY",EDGE,{"derivedFrom":makeQuery(id+"F6.opExtrude","CAP_EDGE",EDGE,{"disambiguationData":[OSD([sQuery(id+"F5.wireOp",EDGE,"E20.3.0.1")])],"isStart":true})});
            var Q64;
            Q64=makeQuery(id+"F6.boolean.opBoolean","COPY",EDGE,{"derivedFrom":makeQuery(id+"F6.opExtrude","CAP_EDGE",EDGE,{"disambiguationData":[OSD([sQuery(id+"F5.wireOp",EDGE,"E20.3.0.2")])],"isStart":true})});
            var Q65;
            Q65=makeQuery(id+"F6.boolean.opBoolean","COPY",EDGE,{"derivedFrom":makeQuery(id+"F6.opExtrude","CAP_EDGE",EDGE,{"disambiguationData":[OSD([sQuery(id+"F5.wireOp",EDGE,"E20.2.0.1")])],"isStart":true})});
            var Q66;
            Q66=makeQuery(id+"F6.boolean.opBoolean","COPY",EDGE,{"derivedFrom":makeQuery(id+"F6.opExtrude","CAP_EDGE",EDGE,{"disambiguationData":[OSD([sQuery(id+"F5.wireOp",EDGE,"E20.2.0.2")])],"isStart":true})});
            var Q67;
            Q67=makeQuery(id+"F6.boolean.opBoolean","COPY",EDGE,{"derivedFrom":makeQuery(id+"F6.opExtrude","CAP_EDGE",EDGE,{"disambiguationData":[OSD([sQuery(id+"F5.wireOp",EDGE,"E20.1.0.1")])],"isStart":true})});
            var Q68;
            Q68=makeQuery(id+"F6.boolean.opBoolean","COPY",EDGE,{"derivedFrom":makeQuery(id+"F6.opExtrude","CAP_EDGE",EDGE,{"disambiguationData":[OSD([sQuery(id+"F5.wireOp",EDGE,"E20.1.0.2")])],"isStart":true})});
            var Q69;
            Q69=makeQuery(id+"F6.boolean.opBoolean","COPY",EDGE,{"derivedFrom":makeQuery(id+"F6.opExtrude","CAP_EDGE",EDGE,{"disambiguationData":[OSD([sQuery(id+"F5.wireOp",EDGE,"E19.0")])],"isStart":true})});
            var Q70;
            Q70=makeQuery(id+"F6.boolean.opBoolean","COPY",EDGE,{"derivedFrom":makeQuery(id+"F6.opExtrude","CAP_EDGE",EDGE,{"disambiguationData":[OSD([sQuery(id+"F5.wireOp",EDGE,"E19.1")])],"isStart":true})});
            var Q71;
            Q71=makeQuery(id+"F6.boolean.opBoolean","COPY",EDGE,{"derivedFrom":makeQuery(id+"F6.opExtrude","CAP_EDGE",EDGE,{"disambiguationData":[OSD([sQuery(id+"F5.wireOp",EDGE,"E18.0.1.1")])],"isStart":true})});
            var Q72;
            Q72=makeQuery(id+"F6.boolean.opBoolean","COPY",EDGE,{"derivedFrom":makeQuery(id+"F6.opExtrude","CAP_EDGE",EDGE,{"disambiguationData":[OSD([sQuery(id+"F5.wireOp",EDGE,"E18.1.1.4")])],"isStart":true})});
            var Q73;
            Q73=makeQuery(id+"F6.boolean.opBoolean","COPY",EDGE,{"derivedFrom":makeQuery(id+"F6.opExtrude","CAP_EDGE",EDGE,{"disambiguationData":[OSD([sQuery(id+"F5.wireOp",EDGE,"E18.1.1.1")])],"isStart":true})});
            var Q74;
            Q74=makeQuery(id+"F6.boolean.opBoolean","COPY",EDGE,{"derivedFrom":makeQuery(id+"F6.opExtrude","CAP_EDGE",EDGE,{"disambiguationData":[OSD([sQuery(id+"F5.wireOp",EDGE,"E18.2.1.4")])],"isStart":true})});
            var Q75;
            Q75=makeQuery(id+"F6.boolean.opBoolean","COPY",EDGE,{"derivedFrom":makeQuery(id+"F6.opExtrude","CAP_EDGE",EDGE,{"disambiguationData":[OSD([sQuery(id+"F5.wireOp",EDGE,"E18.2.1.1")])],"isStart":true})});
            var Q76;
            Q76=makeQuery(id+"F6.boolean.opBoolean","COPY",EDGE,{"derivedFrom":makeQuery(id+"F6.opExtrude","CAP_EDGE",EDGE,{"disambiguationData":[OSD([sQuery(id+"F5.wireOp",EDGE,"E18.3.1.4")])],"isStart":true})});
            var Q77;
            Q77=makeQuery(id+"F6.boolean.opBoolean","COPY",EDGE,{"derivedFrom":makeQuery(id+"F6.opExtrude","CAP_EDGE",EDGE,{"disambiguationData":[OSD([sQuery(id+"F5.wireOp",EDGE,"E18.3.1.1")])],"isStart":true})});
            var Q78;
            Q78=makeQuery(id+"F6.boolean.opBoolean","COPY",EDGE,{"derivedFrom":makeQuery(id+"F6.opExtrude","CAP_EDGE",EDGE,{"disambiguationData":[OSD([sQuery(id+"F5.wireOp",EDGE,"E18.4.1.4")])],"isStart":true})});
            var Q79;
            {var subQ0=sQuery(id+"F5.wireOp",EDGE,"E16.1");Q79=makeQuery(id+"F6.boolean.opBoolean","COPY",EDGE,{"derivedFrom":makeQuery(id+"F6.opExtrude","CAP_EDGE",EDGE,{"disambiguationData":[OSD([subQ0]),TDD([makeQuery(id+"F5.imprint","IMPRINT",EDGE,{"disambiguationData":[TD([[makeQuery(id+"F5.imprint","INTERSECT",VERTEX,{"derivedFrom":[subQ0,sQuery(id+"F5.wireOp",EDGE,"E18.4.1.0"),sQuery(id+"F5.wireOp",EDGE,"E18.4.1.5")]}),-1.0]])],"derivedFrom":subQ0})])],"isStart":true})});}
            var Q80;
            Q80=makeQuery(id+"F6.boolean.opBoolean","COPY",EDGE,{"derivedFrom":makeQuery(id+"F6.opExtrude","CAP_EDGE",EDGE,{"disambiguationData":[OSD([sQuery(id+"F5.wireOp",EDGE,"E18.4.1.5")])],"isStart":true})});
            var Q81;
            Q81=makeQuery(id+"F6.boolean.opBoolean","COPY",EDGE,{"derivedFrom":makeQuery(id+"F6.opExtrude","CAP_EDGE",EDGE,{"disambiguationData":[OSD([sQuery(id+"F5.wireOp",EDGE,"E18.3.1.0")])],"isStart":true})});
            var Q82;
            Q82=makeQuery(id+"F6.boolean.opBoolean","COPY",EDGE,{"derivedFrom":makeQuery(id+"F6.opExtrude","CAP_EDGE",EDGE,{"disambiguationData":[OSD([sQuery(id+"F5.wireOp",EDGE,"E18.3.1.5")])],"isStart":true})});
            var Q83;
            Q83=makeQuery(id+"F6.boolean.opBoolean","COPY",EDGE,{"derivedFrom":makeQuery(id+"F6.opExtrude","CAP_EDGE",EDGE,{"disambiguationData":[OSD([sQuery(id+"F5.wireOp",EDGE,"E18.2.1.0")])],"isStart":true})});
            var Q84;
            Q84=makeQuery(id+"F6.boolean.opBoolean","COPY",EDGE,{"derivedFrom":makeQuery(id+"F6.opExtrude","CAP_EDGE",EDGE,{"disambiguationData":[OSD([sQuery(id+"F5.wireOp",EDGE,"E18.2.1.5")])],"isStart":true})});
            var Q85;
            Q85=makeQuery(id+"F6.boolean.opBoolean","COPY",EDGE,{"derivedFrom":makeQuery(id+"F6.opExtrude","CAP_EDGE",EDGE,{"disambiguationData":[OSD([sQuery(id+"F5.wireOp",EDGE,"E18.1.1.0")])],"isStart":true})});
            var Q86;
            Q86=makeQuery(id+"F6.boolean.opBoolean","COPY",EDGE,{"derivedFrom":makeQuery(id+"F6.opExtrude","CAP_EDGE",EDGE,{"disambiguationData":[OSD([sQuery(id+"F5.wireOp",EDGE,"E18.1.1.5")])],"isStart":true})});
            var Q87;
            Q87=makeQuery(id+"F6.boolean.opBoolean","COPY",EDGE,{"derivedFrom":makeQuery(id+"F6.opExtrude","CAP_EDGE",EDGE,{"disambiguationData":[OSD([sQuery(id+"F5.wireOp",EDGE,"E18.0.1.2")])],"isStart":true})});
            var Q88;
            Q88=makeQuery(id+"F6.boolean.opBoolean","COPY",EDGE,{"derivedFrom":makeQuery(id+"F6.opExtrude","CAP_EDGE",EDGE,{"disambiguationData":[OSD([sQuery(id+"F5.wireOp",EDGE,"E18.1.1.3")])],"isStart":true})});
            var Q89;
            Q89=makeQuery(id+"F6.boolean.opBoolean","COPY",EDGE,{"derivedFrom":makeQuery(id+"F6.opExtrude","CAP_EDGE",EDGE,{"disambiguationData":[OSD([sQuery(id+"F5.wireOp",EDGE,"E18.1.1.2")])],"isStart":true})});
            var Q90;
            Q90=makeQuery(id+"F6.boolean.opBoolean","COPY",EDGE,{"derivedFrom":makeQuery(id+"F6.opExtrude","CAP_EDGE",EDGE,{"disambiguationData":[OSD([sQuery(id+"F5.wireOp",EDGE,"E18.2.1.3")])],"isStart":true})});
            var Q91;
            Q91=makeQuery(id+"F6.boolean.opBoolean","COPY",EDGE,{"derivedFrom":makeQuery(id+"F6.opExtrude","CAP_EDGE",EDGE,{"disambiguationData":[OSD([sQuery(id+"F5.wireOp",EDGE,"E18.2.1.2")])],"isStart":true})});
            var Q92;
            Q92=makeQuery(id+"F6.boolean.opBoolean","COPY",EDGE,{"derivedFrom":makeQuery(id+"F6.opExtrude","CAP_EDGE",EDGE,{"disambiguationData":[OSD([sQuery(id+"F5.wireOp",EDGE,"E18.3.1.3")])],"isStart":true})});
            var Q93;
            Q93=makeQuery(id+"F6.boolean.opBoolean","COPY",EDGE,{"derivedFrom":makeQuery(id+"F6.opExtrude","CAP_EDGE",EDGE,{"disambiguationData":[OSD([sQuery(id+"F5.wireOp",EDGE,"E18.3.1.2")])],"isStart":true})});
            var Q94;
            Q94=makeQuery(id+"F6.boolean.opBoolean","COPY",EDGE,{"derivedFrom":makeQuery(id+"F6.opExtrude","CAP_EDGE",EDGE,{"disambiguationData":[OSD([sQuery(id+"F5.wireOp",EDGE,"E18.4.1.3")])],"isStart":true})});
            var Q95;
            Q95=makeQuery(id+"F6.boolean.opBoolean","COPY",EDGE,{"derivedFrom":makeQuery(id+"F6.opExtrude","CAP_EDGE",EDGE,{"disambiguationData":[OSD([sQuery(id+"F5.wireOp",EDGE,"E20.3.1.5")])],"isStart":true})});
            var Q96;
            Q96=makeQuery(id+"F6.boolean.opBoolean","COPY",EDGE,{"derivedFrom":makeQuery(id+"F6.opExtrude","CAP_EDGE",EDGE,{"disambiguationData":[OSD([sQuery(id+"F5.wireOp",EDGE,"E20.3.1.4")])],"isStart":true})});
            var Q97;
            Q97=makeQuery(id+"F6.boolean.opBoolean","COPY",EDGE,{"derivedFrom":makeQuery(id+"F6.opExtrude","CAP_EDGE",EDGE,{"disambiguationData":[OSD([sQuery(id+"F5.wireOp",EDGE,"E20.2.1.5")])],"isStart":true})});
            var Q98;
            Q98=makeQuery(id+"F6.boolean.opBoolean","COPY",EDGE,{"derivedFrom":makeQuery(id+"F6.opExtrude","CAP_EDGE",EDGE,{"disambiguationData":[OSD([sQuery(id+"F5.wireOp",EDGE,"E20.2.1.4")])],"isStart":true})});
            var Q99;
            Q99=makeQuery(id+"F6.boolean.opBoolean","COPY",EDGE,{"derivedFrom":makeQuery(id+"F6.opExtrude","CAP_EDGE",EDGE,{"disambiguationData":[OSD([sQuery(id+"F5.wireOp",EDGE,"E20.1.1.5")])],"isStart":true})});
            var Q100;
            Q100=makeQuery(id+"F6.boolean.opBoolean","COPY",EDGE,{"derivedFrom":makeQuery(id+"F6.opExtrude","CAP_EDGE",EDGE,{"disambiguationData":[OSD([sQuery(id+"F5.wireOp",EDGE,"E20.1.1.4")])],"isStart":true})});
            var Q101;
            Q101=makeQuery(id+"F6.boolean.opBoolean","COPY",EDGE,{"derivedFrom":makeQuery(id+"F6.opExtrude","CAP_EDGE",EDGE,{"disambiguationData":[OSD([sQuery(id+"F5.wireOp",EDGE,"E20.0.1.5")])],"isStart":true})});
            var Q102;
            Q102=makeQuery(id+"F6.boolean.opBoolean","COPY",EDGE,{"derivedFrom":makeQuery(id+"F6.opExtrude","CAP_EDGE",EDGE,{"disambiguationData":[OSD([sQuery(id+"F5.wireOp",EDGE,"E20.0.1.4")])],"isStart":true})});
            var Q103;
            Q103=makeQuery(id+"F6.boolean.opBoolean","COPY",EDGE,{"derivedFrom":makeQuery(id+"F6.opExtrude","CAP_EDGE",EDGE,{"disambiguationData":[OSD([sQuery(id+"F5.wireOp",EDGE,"E20.0.1.3")])],"isStart":true})});
            var Q104;
            Q104=makeQuery(id+"F6.boolean.opBoolean","COPY",EDGE,{"derivedFrom":makeQuery(id+"F6.opExtrude","CAP_EDGE",EDGE,{"disambiguationData":[OSD([sQuery(id+"F5.wireOp",EDGE,"E20.0.1.0")])],"isStart":true})});
            var Q105;
            Q105=makeQuery(id+"F6.boolean.opBoolean","COPY",EDGE,{"derivedFrom":makeQuery(id+"F6.opExtrude","CAP_EDGE",EDGE,{"disambiguationData":[OSD([sQuery(id+"F5.wireOp",EDGE,"E20.1.1.3")])],"isStart":true})});
            var Q106;
            Q106=makeQuery(id+"F6.boolean.opBoolean","COPY",EDGE,{"derivedFrom":makeQuery(id+"F6.opExtrude","CAP_EDGE",EDGE,{"disambiguationData":[OSD([sQuery(id+"F5.wireOp",EDGE,"E20.1.1.0")])],"isStart":true})});
            var Q107;
            Q107=makeQuery(id+"F6.boolean.opBoolean","COPY",EDGE,{"derivedFrom":makeQuery(id+"F6.opExtrude","CAP_EDGE",EDGE,{"disambiguationData":[OSD([sQuery(id+"F5.wireOp",EDGE,"E20.2.1.3")])],"isStart":true})});
            var Q108;
            Q108=makeQuery(id+"F6.boolean.opBoolean","COPY",EDGE,{"derivedFrom":makeQuery(id+"F6.opExtrude","CAP_EDGE",EDGE,{"disambiguationData":[OSD([sQuery(id+"F5.wireOp",EDGE,"E20.2.1.0")])],"isStart":true})});
            var Q109;
            Q109=makeQuery(id+"F6.boolean.opBoolean","COPY",EDGE,{"derivedFrom":makeQuery(id+"F6.opExtrude","CAP_EDGE",EDGE,{"disambiguationData":[OSD([sQuery(id+"F5.wireOp",EDGE,"E20.3.1.3")])],"isStart":true})});
            var Q110;
            Q110=makeQuery(id+"F6.boolean.opBoolean","COPY",EDGE,{"derivedFrom":makeQuery(id+"F6.opExtrude","CAP_EDGE",EDGE,{"disambiguationData":[OSD([sQuery(id+"F5.wireOp",EDGE,"E20.3.1.0")])],"isStart":true})});
            var Q111;
            Q111=makeQuery(id+"F6.boolean.opBoolean","COPY",EDGE,{"derivedFrom":makeQuery(id+"F6.opExtrude","CAP_EDGE",EDGE,{"disambiguationData":[OSD([sQuery(id+"F5.wireOp",EDGE,"E20.3.1.1")])],"isStart":true})});
            var Q112;
            Q112=makeQuery(id+"F6.boolean.opBoolean","COPY",EDGE,{"derivedFrom":makeQuery(id+"F6.opExtrude","CAP_EDGE",EDGE,{"disambiguationData":[OSD([sQuery(id+"F5.wireOp",EDGE,"E20.3.1.2")])],"isStart":true})});
            var Q113;
            Q113=makeQuery(id+"F6.boolean.opBoolean","COPY",EDGE,{"derivedFrom":makeQuery(id+"F6.opExtrude","CAP_EDGE",EDGE,{"disambiguationData":[OSD([sQuery(id+"F5.wireOp",EDGE,"E20.2.1.1")])],"isStart":true})});
            var Q114;
            Q114=makeQuery(id+"F6.boolean.opBoolean","COPY",EDGE,{"derivedFrom":makeQuery(id+"F6.opExtrude","CAP_EDGE",EDGE,{"disambiguationData":[OSD([sQuery(id+"F5.wireOp",EDGE,"E20.2.1.2")])],"isStart":true})});
            var Q115;
            Q115=makeQuery(id+"F6.boolean.opBoolean","COPY",EDGE,{"derivedFrom":makeQuery(id+"F6.opExtrude","CAP_EDGE",EDGE,{"disambiguationData":[OSD([sQuery(id+"F5.wireOp",EDGE,"E20.1.1.1")])],"isStart":true})});
            var Q116;
            Q116=makeQuery(id+"F6.boolean.opBoolean","COPY",EDGE,{"derivedFrom":makeQuery(id+"F6.opExtrude","CAP_EDGE",EDGE,{"disambiguationData":[OSD([sQuery(id+"F5.wireOp",EDGE,"E20.1.1.2")])],"isStart":true})});
            var Q117;
            Q117=makeQuery(id+"F6.boolean.opBoolean","COPY",EDGE,{"derivedFrom":makeQuery(id+"F6.opExtrude","CAP_EDGE",EDGE,{"disambiguationData":[OSD([sQuery(id+"F5.wireOp",EDGE,"E20.0.1.1")])],"isStart":true})});
            var Q118;
            Q118=makeQuery(id+"F6.boolean.opBoolean","COPY",EDGE,{"derivedFrom":makeQuery(id+"F6.opExtrude","CAP_EDGE",EDGE,{"disambiguationData":[OSD([sQuery(id+"F5.wireOp",EDGE,"E20.0.1.2")])],"isStart":true})});
            var Q119;
            Q119=makeQuery(id+"F6.boolean.opBoolean","COPY",EDGE,{"derivedFrom":makeQuery(id+"F6.opExtrude","CAP_EDGE",EDGE,{"disambiguationData":[OSD([sQuery(id+"F5.wireOp",EDGE,"E18.0.2.0")])],"isStart":true})});
            var Q120;
            Q120=makeQuery(id+"F6.boolean.opBoolean","COPY",EDGE,{"derivedFrom":makeQuery(id+"F6.opExtrude","CAP_EDGE",EDGE,{"disambiguationData":[OSD([sQuery(id+"F5.wireOp",EDGE,"E18.1.2.0")])],"isStart":true})});
            var Q121;
            Q121=makeQuery(id+"F6.boolean.opBoolean","COPY",EDGE,{"derivedFrom":makeQuery(id+"F6.opExtrude","CAP_EDGE",EDGE,{"disambiguationData":[OSD([sQuery(id+"F5.wireOp",EDGE,"E18.2.2.5")])],"isStart":true})});
            var Q122;
            Q122=makeQuery(id+"F6.boolean.opBoolean","COPY",EDGE,{"derivedFrom":makeQuery(id+"F6.opExtrude","CAP_EDGE",EDGE,{"disambiguationData":[OSD([sQuery(id+"F5.wireOp",EDGE,"E18.2.2.0")])],"isStart":true})});
            var Q123;
            Q123=makeQuery(id+"F6.boolean.opBoolean","COPY",EDGE,{"derivedFrom":makeQuery(id+"F6.opExtrude","CAP_EDGE",EDGE,{"disambiguationData":[OSD([sQuery(id+"F5.wireOp",EDGE,"E18.3.2.5")])],"isStart":true})});
            var Q124;
            Q124=makeQuery(id+"F6.boolean.opBoolean","COPY",EDGE,{"derivedFrom":makeQuery(id+"F6.opExtrude","CAP_EDGE",EDGE,{"disambiguationData":[OSD([sQuery(id+"F5.wireOp",EDGE,"E18.3.2.0")])],"isStart":true})});
            var Q125;
            Q125=makeQuery(id+"F6.boolean.opBoolean","COPY",EDGE,{"derivedFrom":makeQuery(id+"F6.opExtrude","CAP_EDGE",EDGE,{"disambiguationData":[OSD([sQuery(id+"F5.wireOp",EDGE,"E18.4.2.5")])],"isStart":true})});
            var Q126;
            {var subQ0=sQuery(id+"F5.wireOp",EDGE,"E16.1");Q126=makeQuery(id+"F6.boolean.opBoolean","COPY",EDGE,{"derivedFrom":makeQuery(id+"F6.opExtrude","CAP_EDGE",EDGE,{"disambiguationData":[OSD([subQ0]),TDD([makeQuery(id+"F5.imprint","IMPRINT",EDGE,{"disambiguationData":[TD([[makeQuery(id+"F5.imprint","INTERSECT",VERTEX,{"derivedFrom":[subQ0,sQuery(id+"F5.wireOp",EDGE,"E18.4.2.0"),sQuery(id+"F5.wireOp",EDGE,"E18.4.2.5")]}),-1.0]])],"derivedFrom":subQ0})])],"isStart":true})});}
            var Q127;
            Q127=makeQuery(id+"F6.boolean.opBoolean","COPY",EDGE,{"derivedFrom":makeQuery(id+"F6.opExtrude","CAP_EDGE",EDGE,{"disambiguationData":[OSD([sQuery(id+"F5.wireOp",EDGE,"E18.4.2.3")])],"isStart":true})});
            var Q128;
            Q128=makeQuery(id+"F6.boolean.opBoolean","COPY",EDGE,{"derivedFrom":makeQuery(id+"F6.opExtrude","CAP_EDGE",EDGE,{"disambiguationData":[OSD([sQuery(id+"F5.wireOp",EDGE,"E18.4.2.4")])],"isStart":true})});
            var Q129;
            Q129=makeQuery(id+"F6.boolean.opBoolean","COPY",EDGE,{"derivedFrom":makeQuery(id+"F6.opExtrude","CAP_EDGE",EDGE,{"disambiguationData":[OSD([sQuery(id+"F5.wireOp",EDGE,"E18.3.2.1")])],"isStart":true})});
            var Q130;
            Q130=makeQuery(id+"F6.boolean.opBoolean","COPY",EDGE,{"derivedFrom":makeQuery(id+"F6.opExtrude","CAP_EDGE",EDGE,{"disambiguationData":[OSD([sQuery(id+"F5.wireOp",EDGE,"E18.3.2.2")])],"isStart":true})});
            var Q131;
            Q131=makeQuery(id+"F6.boolean.opBoolean","COPY",EDGE,{"derivedFrom":makeQuery(id+"F6.opExtrude","CAP_EDGE",EDGE,{"disambiguationData":[OSD([sQuery(id+"F5.wireOp",EDGE,"E18.3.2.3")])],"isStart":true})});
            var Q132;
            Q132=makeQuery(id+"F6.boolean.opBoolean","COPY",EDGE,{"derivedFrom":makeQuery(id+"F6.opExtrude","CAP_EDGE",EDGE,{"disambiguationData":[OSD([sQuery(id+"F5.wireOp",EDGE,"E18.3.2.4")])],"isStart":true})});
            var Q133;
            Q133=makeQuery(id+"F6.boolean.opBoolean","COPY",EDGE,{"derivedFrom":makeQuery(id+"F6.opExtrude","CAP_EDGE",EDGE,{"disambiguationData":[OSD([sQuery(id+"F5.wireOp",EDGE,"E18.2.2.1")])],"isStart":true})});
            var Q134;
            Q134=makeQuery(id+"F6.boolean.opBoolean","COPY",EDGE,{"derivedFrom":makeQuery(id+"F6.opExtrude","CAP_EDGE",EDGE,{"disambiguationData":[OSD([sQuery(id+"F5.wireOp",EDGE,"E18.2.2.2")])],"isStart":true})});
            var Q135;
            Q135=makeQuery(id+"F6.boolean.opBoolean","COPY",EDGE,{"derivedFrom":makeQuery(id+"F6.opExtrude","CAP_EDGE",EDGE,{"disambiguationData":[OSD([sQuery(id+"F5.wireOp",EDGE,"E18.2.2.3")])],"isStart":true})});
            var Q136;
            Q136=makeQuery(id+"F6.boolean.opBoolean","COPY",EDGE,{"derivedFrom":makeQuery(id+"F6.opExtrude","CAP_EDGE",EDGE,{"disambiguationData":[OSD([sQuery(id+"F5.wireOp",EDGE,"E18.2.2.4")])],"isStart":true})});
            var Q137;
            Q137=makeQuery(id+"F6.boolean.opBoolean","COPY",EDGE,{"derivedFrom":makeQuery(id+"F6.opExtrude","CAP_EDGE",EDGE,{"disambiguationData":[OSD([sQuery(id+"F5.wireOp",EDGE,"E18.1.2.1")])],"isStart":true})});
            var Q138;
            Q138=makeQuery(id+"F6.boolean.opBoolean","COPY",EDGE,{"derivedFrom":makeQuery(id+"F6.opExtrude","CAP_EDGE",EDGE,{"disambiguationData":[OSD([sQuery(id+"F5.wireOp",EDGE,"E18.1.2.2")])],"isStart":true})});
            var Q139;
            Q139=makeQuery(id+"F6.boolean.opBoolean","COPY",EDGE,{"derivedFrom":makeQuery(id+"F6.opExtrude","CAP_EDGE",EDGE,{"disambiguationData":[OSD([sQuery(id+"F5.wireOp",EDGE,"E18.1.2.3")])],"isStart":true})});
            var Q140;
            Q140=makeQuery(id+"F6.boolean.opBoolean","COPY",EDGE,{"derivedFrom":makeQuery(id+"F6.opExtrude","CAP_EDGE",EDGE,{"disambiguationData":[OSD([sQuery(id+"F5.wireOp",EDGE,"E18.1.2.4")])],"isStart":true})});
            var Q141;
            Q141=makeQuery(id+"F6.boolean.opBoolean","COPY",EDGE,{"derivedFrom":makeQuery(id+"F6.opExtrude","CAP_EDGE",EDGE,{"disambiguationData":[OSD([sQuery(id+"F5.wireOp",EDGE,"E18.0.2.1")])],"isStart":true})});
            var Q142;
            Q142=makeQuery(id+"F6.boolean.opBoolean","COPY",EDGE,{"derivedFrom":makeQuery(id+"F6.opExtrude","CAP_EDGE",EDGE,{"disambiguationData":[OSD([sQuery(id+"F5.wireOp",EDGE,"E18.0.2.2")])],"isStart":true})});
            var Q143;
            {var subQ0=sQuery(id+"F5.wireOp",EDGE,"E16.0");Q143=makeQuery(id+"F6.boolean.opBoolean","COPY",EDGE,{"derivedFrom":makeQuery(id+"F6.opExtrude","CAP_EDGE",EDGE,{"disambiguationData":[OSD([subQ0]),TDD([makeQuery(id+"F5.imprint","IMPRINT",EDGE,{"disambiguationData":[TD([[makeQuery(id+"F5.imprint","INTERSECT",VERTEX,{"derivedFrom":[subQ0,sQuery(id+"F5.wireOp",EDGE,"E18.0.2.0"),sQuery(id+"F5.wireOp",EDGE,"E18.0.2.5")]}),-1.0]])],"derivedFrom":subQ0})])],"isStart":true})});}
            var Q144;
            Q144=makeQuery(id+"F6.boolean.opBoolean","COPY",EDGE,{"derivedFrom":makeQuery(id+"F6.opExtrude","CAP_EDGE",EDGE,{"disambiguationData":[OSD([sQuery(id+"F5.wireOp",EDGE,"E20.0.2.4")])],"isStart":true})});
            var Q145;
            Q145=makeQuery(id+"F6.boolean.opBoolean","COPY",EDGE,{"derivedFrom":makeQuery(id+"F6.opExtrude","CAP_EDGE",EDGE,{"disambiguationData":[OSD([sQuery(id+"F5.wireOp",EDGE,"E20.0.2.5")])],"isStart":true})});
            var Q146;
            Q146=makeQuery(id+"F6.boolean.opBoolean","COPY",EDGE,{"derivedFrom":makeQuery(id+"F6.opExtrude","CAP_EDGE",EDGE,{"disambiguationData":[OSD([sQuery(id+"F5.wireOp",EDGE,"E20.1.2.4")])],"isStart":true})});
            var Q147;
            Q147=makeQuery(id+"F6.boolean.opBoolean","COPY",EDGE,{"derivedFrom":makeQuery(id+"F6.opExtrude","CAP_EDGE",EDGE,{"disambiguationData":[OSD([sQuery(id+"F5.wireOp",EDGE,"E20.1.2.5")])],"isStart":true})});
            var Q148;
            Q148=makeQuery(id+"F6.boolean.opBoolean","COPY",EDGE,{"derivedFrom":makeQuery(id+"F6.opExtrude","CAP_EDGE",EDGE,{"disambiguationData":[OSD([sQuery(id+"F5.wireOp",EDGE,"E20.2.2.4")])],"isStart":true})});
            var Q149;
            Q149=makeQuery(id+"F6.boolean.opBoolean","COPY",EDGE,{"derivedFrom":makeQuery(id+"F6.opExtrude","CAP_EDGE",EDGE,{"disambiguationData":[OSD([sQuery(id+"F5.wireOp",EDGE,"E20.2.2.5")])],"isStart":true})});
            var Q150;
            Q150=makeQuery(id+"F6.boolean.opBoolean","COPY",EDGE,{"derivedFrom":makeQuery(id+"F6.opExtrude","CAP_EDGE",EDGE,{"disambiguationData":[OSD([sQuery(id+"F5.wireOp",EDGE,"E20.3.2.4")])],"isStart":true})});
            var Q151;
            Q151=makeQuery(id+"F6.boolean.opBoolean","COPY",EDGE,{"derivedFrom":makeQuery(id+"F6.opExtrude","CAP_EDGE",EDGE,{"disambiguationData":[OSD([sQuery(id+"F5.wireOp",EDGE,"E20.3.2.5")])],"isStart":true})});
            var Q152;
            Q152=makeQuery(id+"F6.boolean.opBoolean","COPY",EDGE,{"derivedFrom":makeQuery(id+"F6.opExtrude","CAP_EDGE",EDGE,{"disambiguationData":[OSD([sQuery(id+"F5.wireOp",EDGE,"E20.3.2.0")])],"isStart":true})});
            var Q153;
            Q153=makeQuery(id+"F6.boolean.opBoolean","COPY",EDGE,{"derivedFrom":makeQuery(id+"F6.opExtrude","CAP_EDGE",EDGE,{"disambiguationData":[OSD([sQuery(id+"F5.wireOp",EDGE,"E20.3.2.3")])],"isStart":true})});
            var Q154;
            Q154=makeQuery(id+"F6.boolean.opBoolean","COPY",EDGE,{"derivedFrom":makeQuery(id+"F6.opExtrude","CAP_EDGE",EDGE,{"disambiguationData":[OSD([sQuery(id+"F5.wireOp",EDGE,"E20.2.2.0")])],"isStart":true})});
            var Q155;
            Q155=makeQuery(id+"F6.boolean.opBoolean","COPY",EDGE,{"derivedFrom":makeQuery(id+"F6.opExtrude","CAP_EDGE",EDGE,{"disambiguationData":[OSD([sQuery(id+"F5.wireOp",EDGE,"E20.2.2.3")])],"isStart":true})});
            var Q156;
            Q156=makeQuery(id+"F6.boolean.opBoolean","COPY",EDGE,{"derivedFrom":makeQuery(id+"F6.opExtrude","CAP_EDGE",EDGE,{"disambiguationData":[OSD([sQuery(id+"F5.wireOp",EDGE,"E20.1.2.0")])],"isStart":true})});
            var Q157;
            Q157=makeQuery(id+"F6.boolean.opBoolean","COPY",EDGE,{"derivedFrom":makeQuery(id+"F6.opExtrude","CAP_EDGE",EDGE,{"disambiguationData":[OSD([sQuery(id+"F5.wireOp",EDGE,"E20.1.2.3")])],"isStart":true})});
            var Q158;
            Q158=makeQuery(id+"F6.boolean.opBoolean","COPY",EDGE,{"derivedFrom":makeQuery(id+"F6.opExtrude","CAP_EDGE",EDGE,{"disambiguationData":[OSD([sQuery(id+"F5.wireOp",EDGE,"E20.0.2.0")])],"isStart":true})});
            var Q159;
            Q159=makeQuery(id+"F6.boolean.opBoolean","COPY",EDGE,{"derivedFrom":makeQuery(id+"F6.opExtrude","CAP_EDGE",EDGE,{"disambiguationData":[OSD([sQuery(id+"F5.wireOp",EDGE,"E20.0.2.3")])],"isStart":true})});
            var Q160;
            Q160=makeQuery(id+"F6.boolean.opBoolean","COPY",EDGE,{"derivedFrom":makeQuery(id+"F6.opExtrude","CAP_EDGE",EDGE,{"disambiguationData":[OSD([sQuery(id+"F5.wireOp",EDGE,"E20.0.2.2")])],"isStart":true})});
            var Q161;
            Q161=makeQuery(id+"F6.boolean.opBoolean","COPY",EDGE,{"derivedFrom":makeQuery(id+"F6.opExtrude","CAP_EDGE",EDGE,{"disambiguationData":[OSD([sQuery(id+"F5.wireOp",EDGE,"E20.0.2.1")])],"isStart":true})});
            var Q162;
            Q162=makeQuery(id+"F6.boolean.opBoolean","COPY",EDGE,{"derivedFrom":makeQuery(id+"F6.opExtrude","CAP_EDGE",EDGE,{"disambiguationData":[OSD([sQuery(id+"F5.wireOp",EDGE,"E20.1.2.2")])],"isStart":true})});
            var Q163;
            Q163=makeQuery(id+"F6.boolean.opBoolean","COPY",EDGE,{"derivedFrom":makeQuery(id+"F6.opExtrude","CAP_EDGE",EDGE,{"disambiguationData":[OSD([sQuery(id+"F5.wireOp",EDGE,"E20.1.2.1")])],"isStart":true})});
            var Q164;
            Q164=makeQuery(id+"F6.boolean.opBoolean","COPY",EDGE,{"derivedFrom":makeQuery(id+"F6.opExtrude","CAP_EDGE",EDGE,{"disambiguationData":[OSD([sQuery(id+"F5.wireOp",EDGE,"E20.2.2.2")])],"isStart":true})});
            var Q165;
            Q165=makeQuery(id+"F6.boolean.opBoolean","COPY",EDGE,{"derivedFrom":makeQuery(id+"F6.opExtrude","CAP_EDGE",EDGE,{"disambiguationData":[OSD([sQuery(id+"F5.wireOp",EDGE,"E20.2.2.1")])],"isStart":true})});
            var Q166;
            Q166=makeQuery(id+"F6.boolean.opBoolean","COPY",EDGE,{"derivedFrom":makeQuery(id+"F6.opExtrude","CAP_EDGE",EDGE,{"disambiguationData":[OSD([sQuery(id+"F5.wireOp",EDGE,"E20.3.2.2")])],"isStart":true})});
            var Q167;
            Q167=makeQuery(id+"F6.boolean.opBoolean","COPY",EDGE,{"derivedFrom":makeQuery(id+"F6.opExtrude","CAP_EDGE",EDGE,{"disambiguationData":[OSD([sQuery(id+"F5.wireOp",EDGE,"E20.3.2.1")])],"isStart":true})});
            var Q168;
            {var subQ0=sQuery(id+"F5.wireOp",EDGE,"E16.1");Q168=makeQuery(id+"F6.boolean.opBoolean","COPY",EDGE,{"derivedFrom":makeQuery(id+"F6.opExtrude","CAP_EDGE",EDGE,{"disambiguationData":[OSD([subQ0]),TDD([makeQuery(id+"F5.imprint","IMPRINT",EDGE,{"disambiguationData":[TD([[makeQuery(id+"F5.imprint","INTERSECT",VERTEX,{"derivedFrom":[subQ0,sQuery(id+"F5.wireOp",EDGE,"E16.2")]}),1.0]])],"derivedFrom":subQ0})])],"isStart":true})});}
            var Q169;
            Q169=makeQuery(id+"F6.boolean.opBoolean","COPY",EDGE,{"derivedFrom":makeQuery(id+"F6.opExtrude","CAP_EDGE",EDGE,{"disambiguationData":[OSD([sQuery(id+"F5.wireOp",EDGE,"E18.4.3.5")])],"isStart":true})});
            var Q170;
            Q170=makeQuery(id+"F6.boolean.opBoolean","COPY",EDGE,{"derivedFrom":makeQuery(id+"F6.opExtrude","CAP_EDGE",EDGE,{"disambiguationData":[OSD([sQuery(id+"F5.wireOp",EDGE,"E18.4.3.3")])],"isStart":true})});
            var Q171;
            Q171=makeQuery(id+"F6.boolean.opBoolean","COPY",EDGE,{"derivedFrom":makeQuery(id+"F6.opExtrude","CAP_EDGE",EDGE,{"disambiguationData":[OSD([sQuery(id+"F5.wireOp",EDGE,"E18.4.3.4")])],"isStart":true})});
            var Q172;
            Q172=makeQuery(id+"F6.boolean.opBoolean","COPY",EDGE,{"derivedFrom":makeQuery(id+"F6.opExtrude","CAP_EDGE",EDGE,{"disambiguationData":[OSD([sQuery(id+"F5.wireOp",EDGE,"E18.3.3.1")])],"isStart":true})});
            var Q173;
            Q173=makeQuery(id+"F6.boolean.opBoolean","COPY",EDGE,{"derivedFrom":makeQuery(id+"F6.opExtrude","CAP_EDGE",EDGE,{"disambiguationData":[OSD([sQuery(id+"F5.wireOp",EDGE,"E18.3.3.0")])],"isStart":true})});
            var Q174;
            Q174=makeQuery(id+"F6.boolean.opBoolean","COPY",EDGE,{"derivedFrom":makeQuery(id+"F6.opExtrude","CAP_EDGE",EDGE,{"disambiguationData":[OSD([sQuery(id+"F5.wireOp",EDGE,"E18.3.3.5")])],"isStart":true})});
            var Q175;
            Q175=makeQuery(id+"F6.boolean.opBoolean","COPY",EDGE,{"derivedFrom":makeQuery(id+"F6.opExtrude","CAP_EDGE",EDGE,{"disambiguationData":[OSD([sQuery(id+"F5.wireOp",EDGE,"E18.3.3.4")])],"isStart":true})});
            var Q176;
            Q176=makeQuery(id+"F6.boolean.opBoolean","COPY",EDGE,{"derivedFrom":makeQuery(id+"F6.opExtrude","CAP_EDGE",EDGE,{"disambiguationData":[OSD([sQuery(id+"F5.wireOp",EDGE,"E18.3.3.3")])],"isStart":true})});
            var Q177;
            Q177=makeQuery(id+"F6.boolean.opBoolean","COPY",EDGE,{"derivedFrom":makeQuery(id+"F6.opExtrude","CAP_EDGE",EDGE,{"disambiguationData":[OSD([sQuery(id+"F5.wireOp",EDGE,"E18.3.3.2")])],"isStart":true})});
            var Q178;
            Q178=makeQuery(id+"F6.boolean.opBoolean","COPY",EDGE,{"derivedFrom":makeQuery(id+"F6.opExtrude","CAP_EDGE",EDGE,{"disambiguationData":[OSD([sQuery(id+"F5.wireOp",EDGE,"E18.2.3.1")])],"isStart":true})});
            var Q179;
            Q179=makeQuery(id+"F6.boolean.opBoolean","COPY",EDGE,{"derivedFrom":makeQuery(id+"F6.opExtrude","CAP_EDGE",EDGE,{"disambiguationData":[OSD([sQuery(id+"F5.wireOp",EDGE,"E18.2.3.0")])],"isStart":true})});
            var Q180;
            Q180=makeQuery(id+"F6.boolean.opBoolean","COPY",EDGE,{"derivedFrom":makeQuery(id+"F6.opExtrude","CAP_EDGE",EDGE,{"disambiguationData":[OSD([sQuery(id+"F5.wireOp",EDGE,"E18.2.3.5")])],"isStart":true})});
            var Q181;
            Q181=makeQuery(id+"F6.boolean.opBoolean","COPY",EDGE,{"derivedFrom":makeQuery(id+"F6.opExtrude","CAP_EDGE",EDGE,{"disambiguationData":[OSD([sQuery(id+"F5.wireOp",EDGE,"E18.2.3.4")])],"isStart":true})});
            var Q182;
            Q182=makeQuery(id+"F6.boolean.opBoolean","COPY",EDGE,{"derivedFrom":makeQuery(id+"F6.opExtrude","CAP_EDGE",EDGE,{"disambiguationData":[OSD([sQuery(id+"F5.wireOp",EDGE,"E18.2.3.3")])],"isStart":true})});
            var Q183;
            Q183=makeQuery(id+"F6.boolean.opBoolean","COPY",EDGE,{"derivedFrom":makeQuery(id+"F6.opExtrude","CAP_EDGE",EDGE,{"disambiguationData":[OSD([sQuery(id+"F5.wireOp",EDGE,"E18.2.3.2")])],"isStart":true})});
            var Q184;
            Q184=makeQuery(id+"F6.boolean.opBoolean","COPY",EDGE,{"derivedFrom":makeQuery(id+"F6.opExtrude","CAP_EDGE",EDGE,{"disambiguationData":[OSD([sQuery(id+"F5.wireOp",EDGE,"E18.1.3.2")])],"isStart":true})});
            var Q185;
            Q185=makeQuery(id+"F6.boolean.opBoolean","COPY",EDGE,{"derivedFrom":makeQuery(id+"F6.opExtrude","CAP_EDGE",EDGE,{"disambiguationData":[OSD([sQuery(id+"F5.wireOp",EDGE,"E18.1.3.1")])],"isStart":true})});
            var Q186;
            Q186=makeQuery(id+"F6.boolean.opBoolean","COPY",EDGE,{"derivedFrom":makeQuery(id+"F6.opExtrude","CAP_EDGE",EDGE,{"disambiguationData":[OSD([sQuery(id+"F5.wireOp",EDGE,"E18.1.3.0")])],"isStart":true})});
            var Q187;
            Q187=makeQuery(id+"F6.boolean.opBoolean","COPY",EDGE,{"derivedFrom":makeQuery(id+"F6.opExtrude","CAP_EDGE",EDGE,{"disambiguationData":[OSD([sQuery(id+"F5.wireOp",EDGE,"E18.1.3.5")])],"isStart":true})});
            var Q188;
            Q188=makeQuery(id+"F6.boolean.opBoolean","COPY",EDGE,{"derivedFrom":makeQuery(id+"F6.opExtrude","CAP_EDGE",EDGE,{"disambiguationData":[OSD([sQuery(id+"F5.wireOp",EDGE,"E18.1.3.4")])],"isStart":true})});
            var Q189;
            Q189=makeQuery(id+"F6.boolean.opBoolean","COPY",EDGE,{"derivedFrom":makeQuery(id+"F6.opExtrude","CAP_EDGE",EDGE,{"disambiguationData":[OSD([sQuery(id+"F5.wireOp",EDGE,"E18.1.3.3")])],"isStart":true})});
            var Q190;
            Q190=makeQuery(id+"F6.boolean.opBoolean","COPY",EDGE,{"derivedFrom":makeQuery(id+"F6.opExtrude","CAP_EDGE",EDGE,{"disambiguationData":[OSD([sQuery(id+"F5.wireOp",EDGE,"E18.0.3.1")])],"isStart":true})});
            var Q191;
            Q191=makeQuery(id+"F6.boolean.opBoolean","COPY",EDGE,{"derivedFrom":makeQuery(id+"F6.opExtrude","CAP_EDGE",EDGE,{"disambiguationData":[OSD([sQuery(id+"F5.wireOp",EDGE,"E18.0.3.0")])],"isStart":true})});
            var Q192;
            Q192=makeQuery(id+"F6.boolean.opBoolean","COPY",FACE,{"derivedFrom":makeQuery(id+"F6.opExtrude","CAP_FACE",FACE,{"disambiguationData":[OSD([sQuery(id+"F5.wireOp",EDGE,"E20.0.2.0"),sQuery(id+"F5.wireOp",EDGE,"E20.0.2.1"),sQuery(id+"F5.wireOp",EDGE,"E20.0.2.2"),sQuery(id+"F5.wireOp",EDGE,"E20.0.2.3"),sQuery(id+"F5.wireOp",EDGE,"E20.0.2.4"),sQuery(id+"F5.wireOp",EDGE,"E20.0.2.5")])],"isStart":false})});
            var Q193;
            Q193=makeQuery(id+"F6.boolean.opBoolean","COPY",FACE,{"derivedFrom":makeQuery(id+"F6.opExtrude","CAP_FACE",FACE,{"disambiguationData":[OSD([sQuery(id+"F5.wireOp",EDGE,"E20.1.2.0"),sQuery(id+"F5.wireOp",EDGE,"E20.1.2.1"),sQuery(id+"F5.wireOp",EDGE,"E20.1.2.2"),sQuery(id+"F5.wireOp",EDGE,"E20.1.2.3"),sQuery(id+"F5.wireOp",EDGE,"E20.1.2.4"),sQuery(id+"F5.wireOp",EDGE,"E20.1.2.5")])],"isStart":false})});
            var Q194;
            Q194=makeQuery(id+"F6.boolean.opBoolean","COPY",FACE,{"derivedFrom":makeQuery(id+"F6.opExtrude","CAP_FACE",FACE,{"disambiguationData":[OSD([sQuery(id+"F5.wireOp",EDGE,"E20.2.2.0"),sQuery(id+"F5.wireOp",EDGE,"E20.2.2.1"),sQuery(id+"F5.wireOp",EDGE,"E20.2.2.2"),sQuery(id+"F5.wireOp",EDGE,"E20.2.2.3"),sQuery(id+"F5.wireOp",EDGE,"E20.2.2.4"),sQuery(id+"F5.wireOp",EDGE,"E20.2.2.5")])],"isStart":false})});
            var Q195;
            Q195=makeQuery(id+"F6.boolean.opBoolean","COPY",FACE,{"derivedFrom":makeQuery(id+"F6.opExtrude","CAP_FACE",FACE,{"disambiguationData":[OSD([sQuery(id+"F5.wireOp",EDGE,"E20.3.2.0"),sQuery(id+"F5.wireOp",EDGE,"E20.3.2.1"),sQuery(id+"F5.wireOp",EDGE,"E20.3.2.2"),sQuery(id+"F5.wireOp",EDGE,"E20.3.2.3"),sQuery(id+"F5.wireOp",EDGE,"E20.3.2.4"),sQuery(id+"F5.wireOp",EDGE,"E20.3.2.5")])],"isStart":false})});
            var Q196;
            Q196=makeQuery(id+"F6.boolean.opBoolean","COPY",FACE,{"derivedFrom":makeQuery(id+"F6.opExtrude","CAP_FACE",FACE,{"disambiguationData":[OSD([sQuery(id+"F5.wireOp",EDGE,"E16.1"),sQuery(id+"F5.wireOp",EDGE,"E16.2"),sQuery(id+"F5.wireOp",EDGE,"E18.4.3.3"),sQuery(id+"F5.wireOp",EDGE,"E18.4.3.4"),sQuery(id+"F5.wireOp",EDGE,"E18.4.3.5")])],"isStart":false})});
            var Q197;
            Q197=makeQuery(id+"F6.boolean.opBoolean","COPY",FACE,{"derivedFrom":makeQuery(id+"F6.opExtrude","CAP_FACE",FACE,{"disambiguationData":[OSD([sQuery(id+"F5.wireOp",EDGE,"E18.3.3.0"),sQuery(id+"F5.wireOp",EDGE,"E18.3.3.1"),sQuery(id+"F5.wireOp",EDGE,"E18.3.3.2"),sQuery(id+"F5.wireOp",EDGE,"E18.3.3.3"),sQuery(id+"F5.wireOp",EDGE,"E18.3.3.4"),sQuery(id+"F5.wireOp",EDGE,"E18.3.3.5")])],"isStart":false})});
            var Q198;
            Q198=makeQuery(id+"F6.boolean.opBoolean","COPY",FACE,{"derivedFrom":makeQuery(id+"F6.opExtrude","CAP_FACE",FACE,{"disambiguationData":[OSD([sQuery(id+"F5.wireOp",EDGE,"E18.2.3.0"),sQuery(id+"F5.wireOp",EDGE,"E18.2.3.1"),sQuery(id+"F5.wireOp",EDGE,"E18.2.3.2"),sQuery(id+"F5.wireOp",EDGE,"E18.2.3.3"),sQuery(id+"F5.wireOp",EDGE,"E18.2.3.4"),sQuery(id+"F5.wireOp",EDGE,"E18.2.3.5")])],"isStart":false})});
            var Q199;
            Q199=makeQuery(id+"F6.boolean.opBoolean","COPY",FACE,{"derivedFrom":makeQuery(id+"F6.opExtrude","CAP_FACE",FACE,{"disambiguationData":[OSD([sQuery(id+"F5.wireOp",EDGE,"E18.1.3.0"),sQuery(id+"F5.wireOp",EDGE,"E18.1.3.1"),sQuery(id+"F5.wireOp",EDGE,"E18.1.3.2"),sQuery(id+"F5.wireOp",EDGE,"E18.1.3.3"),sQuery(id+"F5.wireOp",EDGE,"E18.1.3.4"),sQuery(id+"F5.wireOp",EDGE,"E18.1.3.5")])],"isStart":false})});
            var Q200;
            Q200=makeQuery(id+"F6.boolean.opBoolean","COPY",FACE,{"derivedFrom":makeQuery(id+"F6.opExtrude","CAP_FACE",FACE,{"disambiguationData":[OSD([sQuery(id+"F5.wireOp",EDGE,"E16.0"),sQuery(id+"F5.wireOp",EDGE,"E16.5"),sQuery(id+"F5.wireOp",EDGE,"E18.0.3.0"),sQuery(id+"F5.wireOp",EDGE,"E18.0.3.1"),sQuery(id+"F5.wireOp",EDGE,"E18.0.3.2")])],"isStart":false})});
            var Q201;
            {var subQ0=sQuery(id+"F5.wireOp",EDGE,"E16.0");Q201=makeQuery(id+"F6.boolean.opBoolean","COPY",EDGE,{"derivedFrom":makeQuery(id+"F6.opExtrude","CAP_EDGE",EDGE,{"disambiguationData":[OSD([subQ0]),TDD([makeQuery(id+"F5.imprint","IMPRINT",EDGE,{"disambiguationData":[TD([[makeQuery(id+"F5.imprint","INTERSECT",VERTEX,{"derivedFrom":[subQ0,sQuery(id+"F5.wireOp",EDGE,"E16.5")]}),1.0]])],"derivedFrom":subQ0})])],"isStart":true})});}
            var Q202;
            Q202=makeQuery(id+"F6.boolean.opBoolean","COPY",EDGE,{"derivedFrom":makeQuery(id+"F6.opExtrude","CAP_EDGE",EDGE,{"disambiguationData":[OSD([sQuery(id+"F5.wireOp",EDGE,"E18.0.3.2")])],"isStart":true})});
            var Q203;
            {var subQ0=sQuery(id+"F5.wireOp",EDGE,"E16.0");Q203=makeQuery(id+"F6.boolean.opBoolean","COPY",EDGE,{"derivedFrom":makeQuery(id+"F6.opExtrude","CAP_EDGE",EDGE,{"disambiguationData":[OSD([subQ0]),TDD([makeQuery(id+"F5.imprint","IMPRINT",EDGE,{"disambiguationData":[TD([[makeQuery(id+"F5.imprint","INTERSECT",VERTEX,{"derivedFrom":[subQ0,sQuery(id+"F5.wireOp",EDGE,"E18.0.1.0"),sQuery(id+"F5.wireOp",EDGE,"E18.0.1.5")]}),-1.0]])],"derivedFrom":subQ0})])],"isStart":true})});}
            var Q204;
            Q204=makeQuery(id+"F6.boolean.opBoolean","COPY",EDGE,{"derivedFrom":makeQuery(id+"F6.opExtrude","CAP_EDGE",EDGE,{"disambiguationData":[OSD([sQuery(id+"F5.wireOp",EDGE,"E18.0.1.0")])],"isStart":true})});
            var Q205;
            Q205=makeQuery(id+"F6.boolean.opBoolean","COPY",FACE,{"derivedFrom":makeQuery(id+"F6.opExtrude","CAP_FACE",FACE,{"disambiguationData":[OSD([sQuery(id+"F5.wireOp",EDGE,"E16.0"),sQuery(id+"F5.wireOp",EDGE,"E18.0.1.0"),sQuery(id+"F5.wireOp",EDGE,"E18.0.1.1"),sQuery(id+"F5.wireOp",EDGE,"E18.0.1.2")])],"isStart":false})});
            fillet(context, id + "F9", {"entities" : qUnion([Q0, Q1, Q2, Q3, Q4, Q5, Q6, Q7, Q8, Q9, Q10, Q11, Q12, Q13, Q14, Q15, Q16, Q17, Q18, Q19, Q20, Q21, Q22, Q23, Q24, Q25, Q26, Q27, Q28, Q29, Q30, Q31, Q32, Q33, Q34, Q35, Q36, Q37, Q38, Q39, Q40, Q41, Q42, Q43, Q44, Q45, Q46, Q47, Q48, Q49, Q50, Q51, Q52, Q53, Q54, Q55, Q56, Q57, Q58, Q59, Q60, Q61, Q62, Q63, Q64, Q65, Q66, Q67, Q68, Q69, Q70, Q71, Q72, Q73, Q74, Q75, Q76, Q77, Q78, Q79, Q80, Q81, Q82, Q83, Q84, Q85, Q86, Q87, Q88, Q89, Q90, Q91, Q92, Q93, Q94, Q95, Q96, Q97, Q98, Q99, Q100, Q101, Q102, Q103, Q104, Q105, Q106, Q107, Q108, Q109, Q110, Q111, Q112, Q113, Q114, Q115, Q116, Q117, Q118, Q119, Q120, Q121, Q122, Q123, Q124, Q125, Q126, Q127, Q128, Q129, Q130, Q131, Q132, Q133, Q134, Q135, Q136, Q137, Q138, Q139, Q140, Q141, Q142, Q143, Q144, Q145, Q146, Q147, Q148, Q149, Q150, Q151, Q152, Q153, Q154, Q155, Q156, Q157, Q158, Q159, Q160, Q161, Q162, Q163, Q164, Q165, Q166, Q167, Q168, Q169, Q170, Q171, Q172, Q173, Q174, Q175, Q176, Q177, Q178, Q179, Q180, Q181, Q182, Q183, Q184, Q185, Q186, Q187, Q188, Q189, Q190, Q191, Q192, Q193, Q194, Q195, Q196, Q197, Q198, Q199, Q200, Q201, Q202, Q203, Q204, Q205]), "radius" : 1 * mm, "tangentPropagation" : true, "allowEdgeOverflow" : false});
        }
    });
